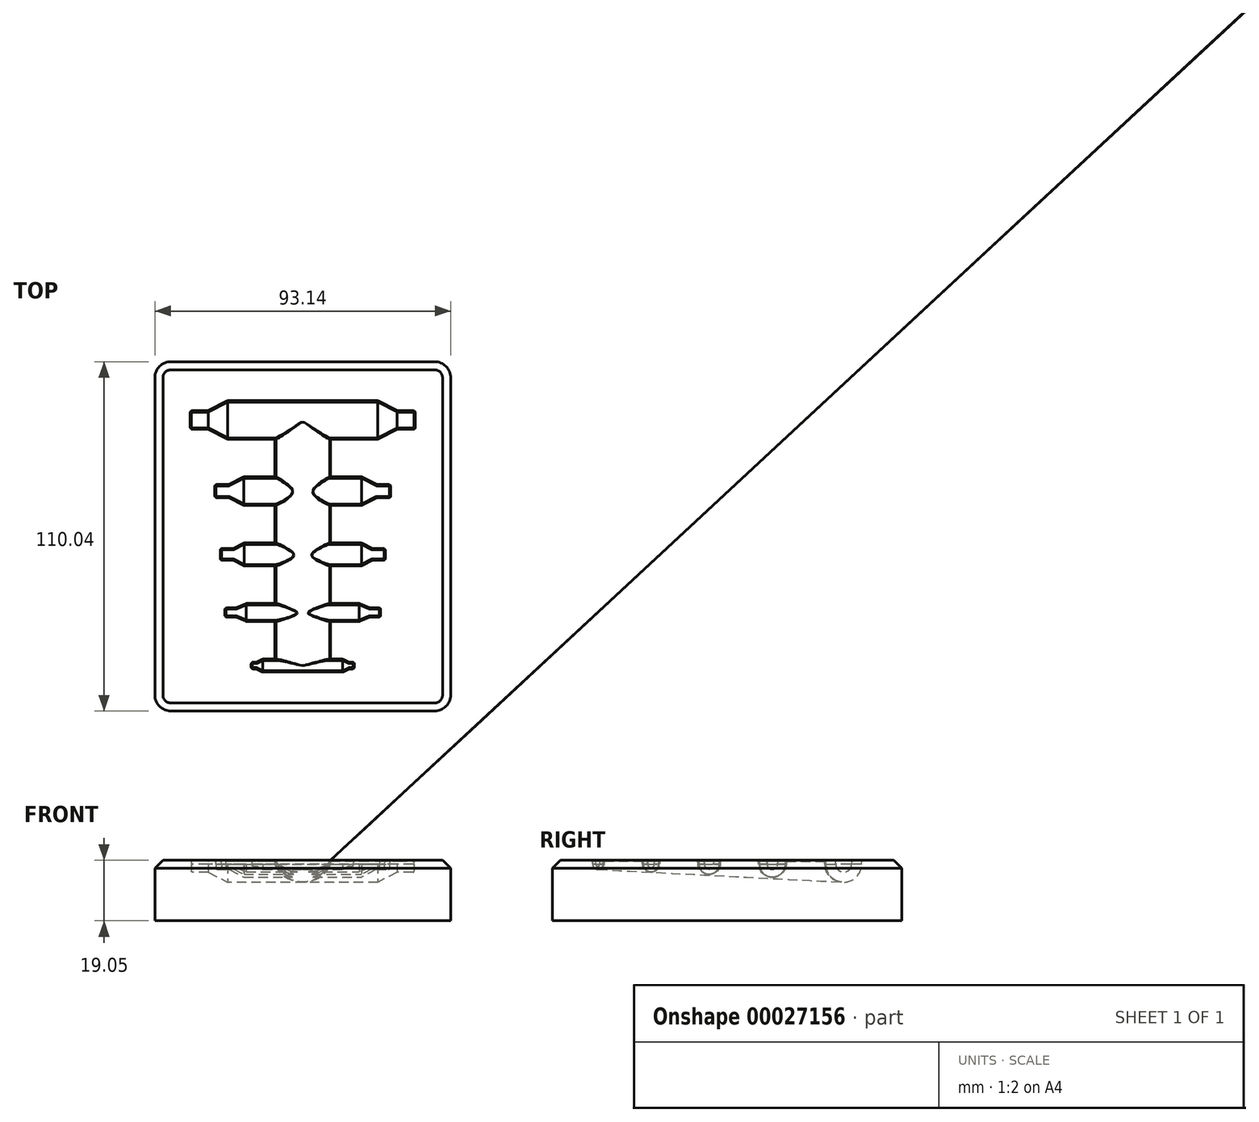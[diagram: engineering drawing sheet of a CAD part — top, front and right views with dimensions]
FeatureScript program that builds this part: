
annotation { "Feature Type Name" : "Feature", "Feature Type Description" : "" }
export const myFeature = defineFeature(function(context is Context, id is Id, definition is map)
    precondition{}
    {
        {
            var Q0;
            Q0=qCreatedBy(makeId("Top.planeOp"),FACE);
            var sketch = newSketch(context, id + "F0", { "sketchPlane" : qUnion([Q0])});
            skLineSegment(sketch, "E0.bottom", {"start": v(-46.57, 55.02) * mm, "end": v(46.57, 55.02) * mm});
            skLineSegment(sketch, "E0.top", {"start": v(-46.57, -55.02) * mm, "end": v(46.57, -55.02) * mm});
            skLineSegment(sketch, "E0.left", {"start": v(-46.57, 55.02) * mm, "end": v(-46.57, -55.02) * mm});
            skLineSegment(sketch, "E0.right", {"start": v(46.57, 55.02) * mm, "end": v(46.57, -55.02) * mm});
            skSolve(sketch);
        }
        {
            var Q0;
            Q0 = qSketchRegion(id + "F0", true);
            extrude(context, id + "F1", {"entities" : qUnion([Q0]), "depth" : 17.78 * mm});
        }
        {
            var Q0;
            Q0=makeQuery(id+"F1.opExtrude","CAP_FACE",FACE,{"disambiguationData":[OSD([sQuery(id+"F0.wireOp",EDGE,"E0.bottom"),sQuery(id+"F0.wireOp",EDGE,"E0.top"),sQuery(id+"F0.wireOp",EDGE,"E0.left"),sQuery(id+"F0.wireOp",EDGE,"E0.right")])],"isStart":false});
            var sketch = newSketch(context, id + "F2", { "sketchPlane" : qUnion([Q0])});
            skLineSegment(sketch, "E1", {"start": v(-15.88, -40.7) * mm, "end": v(-15.88, -41.34) * mm});
            skLineSegment(sketch, "E2", {"start": v(-15.87, -41.34) * mm, "end": v(-14.48, -41.34) * mm});
            skLineSegment(sketch, "E3", {"start": v(-14.48, -41.34) * mm, "end": v(-12.57, -42.32) * mm});
            skLineSegment(sketch, "E4", {"start": v(-12.57, -42.32) * mm, "end": v(0, -42.32) * mm});
            skLineSegment(sketch, "E5.MirrorCS", {"start": v(12.57, -42.32) * mm, "end": v(0, -42.32) * mm});
            skLineSegment(sketch, "E6.MirrorCS", {"start": v(14.48, -41.34) * mm, "end": v(12.57, -42.32) * mm});
            skLineSegment(sketch, "E7.MirrorCS", {"start": v(15.88, -40.7) * mm, "end": v(15.88, -41.34) * mm});
            skLineSegment(sketch, "E8.MirrorCS", {"start": v(15.87, -41.34) * mm, "end": v(14.48, -41.34) * mm});
            skLineSegment(sketch, "E9", {"start": v(-15.87, -40.7) * mm, "end": v(15.87, -40.7) * mm});
            skSolve(sketch);
        }
        {
            var Q0;
            Q0 = qSketchRegion(id + "F2", true);
            var Q1;
            Q1=sQuery(id+"F2.wireOp",EDGE,"E9");
            revolve(context, id + "F3", {"operationType" : NewBodyOperationType.REMOVE, "entities" : qUnion([Q0]), "axis" : qUnion([Q1]), "revolveType" : RevolveType.FULL, "oppositeDirection" : true});
        }
        {
            var Q0;
            Q0=makeQuery(id+"F1.opExtrude","CAP_FACE",FACE,{"disambiguationData":[OSD([sQuery(id+"F0.wireOp",EDGE,"E0.bottom"),sQuery(id+"F0.wireOp",EDGE,"E0.top"),sQuery(id+"F0.wireOp",EDGE,"E0.left"),sQuery(id+"F0.wireOp",EDGE,"E0.right")])],"isStart":false});
            var sketch = newSketch(context, id + "F4", { "sketchPlane" : qUnion([Q0])});
            skLineSegment(sketch, "E10", {"start": v(-24.13, -23.97) * mm, "end": v(-24.13, -25.01) * mm});
            skLineSegment(sketch, "E11", {"start": v(-24.13, -25.01) * mm, "end": v(-20.96, -25.01) * mm});
            skLineSegment(sketch, "E12", {"start": v(-20.96, -25.01) * mm, "end": v(-17.78, -26.38) * mm});
            skLineSegment(sketch, "E13", {"start": v(-17.78, -26.38) * mm, "end": v(0, -26.38) * mm});
            skLineSegment(sketch, "E14.MirrorCS", {"start": v(17.78, -26.38) * mm, "end": v(0, -26.38) * mm});
            skLineSegment(sketch, "E15.MirrorCS", {"start": v(20.96, -25.01) * mm, "end": v(17.78, -26.38) * mm});
            skLineSegment(sketch, "E16.MirrorCS", {"start": v(24.13, -23.97) * mm, "end": v(24.13, -25.01) * mm});
            skLineSegment(sketch, "E17.MirrorCS", {"start": v(24.13, -25.01) * mm, "end": v(20.96, -25.01) * mm});
            skLineSegment(sketch, "E18", {"start": v(-24.13, -23.97) * mm, "end": v(24.13, -23.97) * mm});
            skSolve(sketch);
        }
        {
            var Q0;
            Q0 = qSketchRegion(id + "F4", true);
            var Q1;
            Q1=sQuery(id+"F4.wireOp",EDGE,"E18");
            revolve(context, id + "F5", {"operationType" : NewBodyOperationType.REMOVE, "entities" : qUnion([Q0]), "axis" : qUnion([Q1]), "revolveType" : RevolveType.FULL, "oppositeDirection" : true});
        }
        {
            var Q0;
            Q0=makeQuery(id+"F1.opExtrude","CAP_FACE",FACE,{"disambiguationData":[OSD([sQuery(id+"F0.wireOp",EDGE,"E0.bottom"),sQuery(id+"F0.wireOp",EDGE,"E0.top"),sQuery(id+"F0.wireOp",EDGE,"E0.left"),sQuery(id+"F0.wireOp",EDGE,"E0.right")])],"isStart":false});
            var sketch = newSketch(context, id + "F6", { "sketchPlane" : qUnion([Q0])});
            skLineSegment(sketch, "E19", {"start": v(-25.6, -5.68) * mm, "end": v(-25.6, -7.14) * mm});
            skLineSegment(sketch, "E20", {"start": v(-25.6, -7.14) * mm, "end": v(-21.8, -7.14) * mm});
            skLineSegment(sketch, "E21", {"start": v(-21.8, -7.14) * mm, "end": v(-18.5, -8.86) * mm});
            skLineSegment(sketch, "E22", {"start": v(-18.5, -8.86) * mm, "end": v(0, -8.86) * mm});
            skLineSegment(sketch, "E23.MirrorCS", {"start": v(18.5, -8.86) * mm, "end": v(0, -8.86) * mm});
            skLineSegment(sketch, "E24.MirrorCS", {"start": v(21.8, -7.14) * mm, "end": v(18.5, -8.86) * mm});
            skLineSegment(sketch, "E25.MirrorCS", {"start": v(25.6, -5.68) * mm, "end": v(25.6, -7.14) * mm});
            skLineSegment(sketch, "E26.MirrorCS", {"start": v(25.6, -7.14) * mm, "end": v(21.8, -7.14) * mm});
            skLineSegment(sketch, "E27", {"start": v(-25.6, -5.68) * mm, "end": v(25.6, -5.68) * mm});
            skSolve(sketch);
        }
        {
            var Q0;
            Q0 = qSketchRegion(id + "F6", true);
            var Q1;
            Q1=sQuery(id+"F6.wireOp",EDGE,"E27");
            revolve(context, id + "F7", {"operationType" : NewBodyOperationType.REMOVE, "entities" : qUnion([Q0]), "axis" : qUnion([Q1]), "revolveType" : RevolveType.FULL, "oppositeDirection" : true});
        }
        {
            var Q0;
            Q0=makeQuery(id+"F1.opExtrude","CAP_FACE",FACE,{"disambiguationData":[OSD([sQuery(id+"F0.wireOp",EDGE,"E0.bottom"),sQuery(id+"F0.wireOp",EDGE,"E0.top"),sQuery(id+"F0.wireOp",EDGE,"E0.left"),sQuery(id+"F0.wireOp",EDGE,"E0.right")])],"isStart":false});
            var sketch = newSketch(context, id + "F8", { "sketchPlane" : qUnion([Q0])});
            skLineSegment(sketch, "E28", {"start": v(-27.3, 14.26) * mm, "end": v(-27.3, 12.6) * mm});
            skLineSegment(sketch, "E29", {"start": v(-27.3, 12.6) * mm, "end": v(-23.2, 12.6) * mm});
            skLineSegment(sketch, "E30", {"start": v(-23.2, 12.6) * mm, "end": v(-18.57, 10.2) * mm});
            skLineSegment(sketch, "E31", {"start": v(-18.57, 10.2) * mm, "end": v(0, 10.2) * mm});
            skLineSegment(sketch, "E32.MirrorCS", {"start": v(18.57, 10.2) * mm, "end": v(0, 10.2) * mm});
            skLineSegment(sketch, "E33.MirrorCS", {"start": v(23.2, 12.6) * mm, "end": v(18.57, 10.2) * mm});
            skLineSegment(sketch, "E34.MirrorCS", {"start": v(27.3, 14.26) * mm, "end": v(27.3, 12.6) * mm});
            skLineSegment(sketch, "E35.MirrorCS", {"start": v(27.3, 12.6) * mm, "end": v(23.2, 12.6) * mm});
            skLineSegment(sketch, "E36", {"start": v(-27.3, 14.26) * mm, "end": v(27.3, 14.26) * mm});
            skSolve(sketch);
        }
        {
            var Q0;
            Q0 = qSketchRegion(id + "F8", true);
            var Q1;
            Q1=sQuery(id+"F8.wireOp",EDGE,"E36");
            revolve(context, id + "F9", {"operationType" : NewBodyOperationType.REMOVE, "entities" : qUnion([Q0]), "axis" : qUnion([Q1]), "revolveType" : RevolveType.FULL, "oppositeDirection" : true});
        }
        {
            var Q0;
            Q0=makeQuery(id+"F1.opExtrude","CAP_FACE",FACE,{"disambiguationData":[OSD([sQuery(id+"F0.wireOp",EDGE,"E0.bottom"),sQuery(id+"F0.wireOp",EDGE,"E0.top"),sQuery(id+"F0.wireOp",EDGE,"E0.left"),sQuery(id+"F0.wireOp",EDGE,"E0.right")])],"isStart":false});
            var sketch = newSketch(context, id + "F10", { "sketchPlane" : qUnion([Q0])});
            skLineSegment(sketch, "E37", {"start": v(-35.05, 36.67) * mm, "end": v(-35.05, 34.2) * mm});
            skLineSegment(sketch, "E38", {"start": v(-35.05, 34.2) * mm, "end": v(-29.72, 34.2) * mm});
            skLineSegment(sketch, "E39", {"start": v(-29.72, 34.2) * mm, "end": v(-23.62, 31.02) * mm});
            skLineSegment(sketch, "E40", {"start": v(-23.62, 31.02) * mm, "end": v(0, 31.02) * mm});
            skLineSegment(sketch, "E41.MirrorCS", {"start": v(23.62, 31.02) * mm, "end": v(0, 31.02) * mm});
            skLineSegment(sketch, "E42.MirrorCS", {"start": v(29.72, 34.2) * mm, "end": v(23.62, 31.02) * mm});
            skLineSegment(sketch, "E43.MirrorCS", {"start": v(35.05, 36.67) * mm, "end": v(35.05, 34.2) * mm});
            skLineSegment(sketch, "E44.MirrorCS", {"start": v(35.05, 34.2) * mm, "end": v(29.72, 34.2) * mm});
            skLineSegment(sketch, "E45", {"start": v(-35.05, 36.67) * mm, "end": v(35.05, 36.67) * mm});
            skSolve(sketch);
        }
        {
            var Q0;
            Q0 = qSketchRegion(id + "F10", true);
            var Q1;
            Q1=sQuery(id+"F10.wireOp",EDGE,"E45");
            revolve(context, id + "F11", {"operationType" : NewBodyOperationType.REMOVE, "entities" : qUnion([Q0]), "axis" : qUnion([Q1]), "revolveType" : RevolveType.FULL});
        }
        {
            var Q0;
            Q0=sQuery(id+"F2.wireOp",EDGE,"E9");
            cPlane(context, id + "F12", {"entities" : qUnion([Q0]), "cplaneType" : CPlaneType.LINE_ANGLE, "offset" : 152.4 * mm, "angle" : 0 * degree, "width" : 152.4 * mm, "height" : 152.4 * mm});
        }
        {
            var Q0;
            Q0=sQuery(id+"F10.wireOp",EDGE,"E45");
            cPlane(context, id + "F13", {"entities" : qUnion([Q0]), "cplaneType" : CPlaneType.LINE_ANGLE, "offset" : 152.4 * mm, "angle" : 0 * degree, "width" : 152.4 * mm, "height" : 152.4 * mm});
        }
        {
            var Q0;
            Q0=makeQuery(id+"F1.opExtrude","CAP_FACE",FACE,{"disambiguationData":[OSD([sQuery(id+"F0.wireOp",EDGE,"E0.bottom"),sQuery(id+"F0.wireOp",EDGE,"E0.top"),sQuery(id+"F0.wireOp",EDGE,"E0.left"),sQuery(id+"F0.wireOp",EDGE,"E0.right")])],"isStart":false});
            extrude(context, id + "F14", {"entities" : qUnion([Q0]), "operationType" : NewBodyOperationType.ADD, "depth" : 1.27 * mm, "hasDraft" : true, "draftAngle" : 5 * degree, "draftPullDirection" : true});
        }
        {
            var Q0;
            Q0=qCreatedBy(id+"F12.planeOp",FACE);
            var sketch = newSketch(context, id + "F15", { "sketchPlane" : qUnion([Q0])});
            skEllipse(sketch, "E46", {"center": v(0, 19.05) * mm, "majorRadius": 8.47 * mm, "minorRadius": 2.89 * mm, "majorAxis": v(-1, 0)});
            skSolve(sketch);
        }
        {
            var Q0;
            Q0=qCreatedBy(id+"F13.planeOp",FACE);
            var sketch = newSketch(context, id + "F16", { "sketchPlane" : qUnion([Q0])});
            skEllipse(sketch, "E47", {"center": v(0, 19.05) * mm, "majorRadius": 8.47 * mm, "minorRadius": 6.92 * mm, "majorAxis": v(-1, 0)});
            skSolve(sketch);
        }
        {
            var Q1;
            Q1 = qSketchRegion(id + "F15", true);
            var Q2;
            Q2 = qSketchRegion(id + "F16", true);
            loft(context, id + "F17", {"operationType" : NewBodyOperationType.REMOVE, "sheetProfilesArray" : [{ "sheetProfileEntities" : qUnion([Q1]) }, { "sheetProfileEntities" : qUnion([Q2]) }]});
        }
        {
            var Q0;
            Q0=makeQuery(id+"F1.opExtrude","SWEPT_EDGE",EDGE,{"disambiguationData":[OSD([sQuery(id+"F0.wireOp",EDGE,"E0.top"),sQuery(id+"F0.wireOp",EDGE,"E0.left")])]});
            var Q1;
            Q1=makeQuery(id+"F1.opExtrude","SWEPT_EDGE",EDGE,{"disambiguationData":[OSD([sQuery(id+"F0.wireOp",EDGE,"E0.top"),sQuery(id+"F0.wireOp",EDGE,"E0.right")])]});
            var Q2;
            Q2=makeQuery(id+"F1.opExtrude","SWEPT_EDGE",EDGE,{"disambiguationData":[OSD([sQuery(id+"F0.wireOp",EDGE,"E0.bottom"),sQuery(id+"F0.wireOp",EDGE,"E0.right")])]});
            var Q3;
            Q3=makeQuery(id+"F1.opExtrude","SWEPT_EDGE",EDGE,{"disambiguationData":[OSD([sQuery(id+"F0.wireOp",EDGE,"E0.bottom"),sQuery(id+"F0.wireOp",EDGE,"E0.left")])]});
            var Q4;
            Q4=makeQuery(id+"F14.opExtrude","SWEPT_EDGE",EDGE,{"disambiguationData":[OSD([sQuery(id+"F0.wireOp",EDGE,"E0.top"),sQuery(id+"F0.wireOp",EDGE,"E0.right")])]});
            var Q5;
            Q5=makeQuery(id+"F14.opExtrude","SWEPT_EDGE",EDGE,{"disambiguationData":[OSD([sQuery(id+"F0.wireOp",EDGE,"E0.bottom"),sQuery(id+"F0.wireOp",EDGE,"E0.right")])]});
            var Q6;
            Q6=makeQuery(id+"F14.opExtrude","SWEPT_EDGE",EDGE,{"disambiguationData":[OSD([sQuery(id+"F0.wireOp",EDGE,"E0.bottom"),sQuery(id+"F0.wireOp",EDGE,"E0.left")])]});
            var Q7;
            Q7=makeQuery(id+"F14.opExtrude","SWEPT_EDGE",EDGE,{"disambiguationData":[OSD([sQuery(id+"F0.wireOp",EDGE,"E0.top"),sQuery(id+"F0.wireOp",EDGE,"E0.left")])]});
            fillet(context, id + "F18", {"entities" : qUnion([Q0, Q1, Q2, Q3, Q4, Q5, Q6, Q7]), "radius" : 5.08 * mm, "tangentPropagation" : true, "allowEdgeOverflow" : false});
        }
        {
            var Q0;
            Q0=makeQuery(id+"F14.opExtrude","CAP_EDGE",EDGE,{"disambiguationData":[OSD([sQuery(id+"F0.wireOp",EDGE,"E0.left")])],"isStart":false});
            chamfer(context, id + "F19", {"entities" : qUnion([Q0]), "width" : 2.54 * mm, "tangentPropagation" : true});
        }
        {
            var Q0;
            Q0=makeQuery(id+"F17.boolean.opBoolean","INTERSECT",EDGE,{"disambiguationData":[OD(0.0)],"derivedFrom":[makeQuery(id+"F5.boolean.opBoolean","COPY",FACE,{"derivedFrom":makeQuery(id+"F5.opRevolve","SWEPT_FACE",FACE,{"disambiguationData":[OSD([sQuery(id+"F4.wireOp",EDGE,"E13"),sQuery(id+"F4.wireOp",EDGE,"E14.MirrorCS")])]})}),makeQuery(id+"F17.opLoft","SWEPT_FACE",FACE,{"disambiguationData":[OSD([sQuery(id+"F15.wireOp",EDGE,"E46"),sQuery(id+"F16.wireOp",EDGE,"E47")])]})]});
            var Q1;
            {var subQ0=sQuery(id+"F0.wireOp",EDGE,"E0.bottom");var subQ1=sQuery(id+"F0.wireOp",EDGE,"E0.top");var subQ2=sQuery(id+"F0.wireOp",EDGE,"E0.left");var subQ3=sQuery(id+"F0.wireOp",EDGE,"E0.right");var subQ4=sQuery(id+"F4.wireOp",EDGE,"E13");var subQ5=sQuery(id+"F4.wireOp",EDGE,"E14.MirrorCS");Q1=makeQuery(id+"F17.boolean.opBoolean","INTERSECT",EDGE,{"disambiguationData":[OD(0.0)],"derivedFrom":[makeQuery(id+"F14.opExtrude","SWEPT_FACE",FACE,{"disambiguationData":[OSD([subQ0,subQ1,subQ2,subQ3,subQ4,subQ5]),TDD([makeQuery(id+"F5.boolean.opBoolean","INTERSECT",EDGE,{"disambiguationData":[OD(1.0)],"derivedFrom":[makeQuery(id+"F1.opExtrude","CAP_FACE",FACE,{"disambiguationData":[OSD([subQ0,subQ1,subQ2,subQ3])],"isStart":false}),makeQuery(id+"F5.opRevolve","SWEPT_FACE",FACE,{"disambiguationData":[OSD([subQ4,subQ5])]})]})])]}),makeQuery(id+"F17.opLoft","SWEPT_FACE",FACE,{"disambiguationData":[OSD([sQuery(id+"F15.wireOp",EDGE,"E46"),sQuery(id+"F16.wireOp",EDGE,"E47")])]})]});}
            var Q2;
            {var subQ0=sQuery(id+"F0.wireOp",EDGE,"E0.bottom");var subQ1=sQuery(id+"F0.wireOp",EDGE,"E0.top");var subQ2=sQuery(id+"F0.wireOp",EDGE,"E0.left");var subQ3=sQuery(id+"F0.wireOp",EDGE,"E0.right");var subQ4=sQuery(id+"F4.wireOp",EDGE,"E13");var subQ5=sQuery(id+"F4.wireOp",EDGE,"E14.MirrorCS");Q2=makeQuery(id+"F17.boolean.opBoolean","INTERSECT",EDGE,{"disambiguationData":[OD(0.0)],"derivedFrom":[makeQuery(id+"F14.opExtrude","SWEPT_FACE",FACE,{"disambiguationData":[OSD([subQ0,subQ1,subQ2,subQ3,subQ4,subQ5]),TDD([makeQuery(id+"F5.boolean.opBoolean","INTERSECT",EDGE,{"disambiguationData":[OD(0.0)],"derivedFrom":[makeQuery(id+"F1.opExtrude","CAP_FACE",FACE,{"disambiguationData":[OSD([subQ0,subQ1,subQ2,subQ3])],"isStart":false}),makeQuery(id+"F5.opRevolve","SWEPT_FACE",FACE,{"disambiguationData":[OSD([subQ4,subQ5])]})]})])]}),makeQuery(id+"F17.opLoft","SWEPT_FACE",FACE,{"disambiguationData":[OSD([sQuery(id+"F15.wireOp",EDGE,"E46"),sQuery(id+"F16.wireOp",EDGE,"E47")])]})]});}
            var Q3;
            Q3=makeQuery(id+"F17.boolean.opBoolean","INTERSECT",EDGE,{"derivedFrom":[makeQuery(id+"F3.boolean.opBoolean","COPY",FACE,{"derivedFrom":makeQuery(id+"F3.opRevolve","SWEPT_FACE",FACE,{"disambiguationData":[OSD([sQuery(id+"F2.wireOp",EDGE,"E4"),sQuery(id+"F2.wireOp",EDGE,"E5.MirrorCS")])]})}),makeQuery(id+"F17.opLoft","SWEPT_FACE",FACE,{"disambiguationData":[OSD([sQuery(id+"F15.wireOp",EDGE,"E46"),sQuery(id+"F16.wireOp",EDGE,"E47")])]})]});
            var Q4;
            {var subQ0=sQuery(id+"F0.wireOp",EDGE,"E0.bottom");var subQ1=sQuery(id+"F0.wireOp",EDGE,"E0.top");var subQ2=sQuery(id+"F0.wireOp",EDGE,"E0.left");var subQ3=sQuery(id+"F0.wireOp",EDGE,"E0.right");var subQ4=sQuery(id+"F2.wireOp",EDGE,"E4");var subQ5=sQuery(id+"F2.wireOp",EDGE,"E5.MirrorCS");Q4=makeQuery(id+"F17.boolean.opBoolean","INTERSECT",EDGE,{"disambiguationData":[OD(0.0)],"derivedFrom":[makeQuery(id+"F14.opExtrude","SWEPT_FACE",FACE,{"disambiguationData":[OSD([subQ0,subQ1,subQ2,subQ3,subQ4,subQ5]),TDD([makeQuery(id+"F3.boolean.opBoolean","INTERSECT",EDGE,{"disambiguationData":[OD(1.0)],"derivedFrom":[makeQuery(id+"F1.opExtrude","CAP_FACE",FACE,{"disambiguationData":[OSD([subQ0,subQ1,subQ2,subQ3])],"isStart":false}),makeQuery(id+"F3.opRevolve","SWEPT_FACE",FACE,{"disambiguationData":[OSD([subQ4,subQ5])]})]})])]}),makeQuery(id+"F17.opLoft","SWEPT_FACE",FACE,{"disambiguationData":[OSD([sQuery(id+"F15.wireOp",EDGE,"E46"),sQuery(id+"F16.wireOp",EDGE,"E47")])]})]});}
            var Q5;
            {var subQ0=sQuery(id+"F0.wireOp",EDGE,"E0.bottom");var subQ1=sQuery(id+"F0.wireOp",EDGE,"E0.top");var subQ2=sQuery(id+"F0.wireOp",EDGE,"E0.left");var subQ3=sQuery(id+"F0.wireOp",EDGE,"E0.right");var subQ4=sQuery(id+"F2.wireOp",EDGE,"E4");var subQ5=sQuery(id+"F2.wireOp",EDGE,"E5.MirrorCS");Q5=makeQuery(id+"F17.boolean.opBoolean","INTERSECT",EDGE,{"disambiguationData":[OD(1.0)],"derivedFrom":[makeQuery(id+"F14.opExtrude","SWEPT_FACE",FACE,{"disambiguationData":[OSD([subQ0,subQ1,subQ2,subQ3,subQ4,subQ5]),TDD([makeQuery(id+"F3.boolean.opBoolean","INTERSECT",EDGE,{"disambiguationData":[OD(1.0)],"derivedFrom":[makeQuery(id+"F1.opExtrude","CAP_FACE",FACE,{"disambiguationData":[OSD([subQ0,subQ1,subQ2,subQ3])],"isStart":false}),makeQuery(id+"F3.opRevolve","SWEPT_FACE",FACE,{"disambiguationData":[OSD([subQ4,subQ5])]})]})])]}),makeQuery(id+"F17.opLoft","SWEPT_FACE",FACE,{"disambiguationData":[OSD([sQuery(id+"F15.wireOp",EDGE,"E46"),sQuery(id+"F16.wireOp",EDGE,"E47")])]})]});}
            var Q6;
            Q6=makeQuery(id+"F17.boolean.opBoolean","INTERSECT",EDGE,{"disambiguationData":[OD(1.0)],"derivedFrom":[makeQuery(id+"F5.boolean.opBoolean","COPY",FACE,{"derivedFrom":makeQuery(id+"F5.opRevolve","SWEPT_FACE",FACE,{"disambiguationData":[OSD([sQuery(id+"F4.wireOp",EDGE,"E13"),sQuery(id+"F4.wireOp",EDGE,"E14.MirrorCS")])]})}),makeQuery(id+"F17.opLoft","SWEPT_FACE",FACE,{"disambiguationData":[OSD([sQuery(id+"F15.wireOp",EDGE,"E46"),sQuery(id+"F16.wireOp",EDGE,"E47")])]})]});
            var Q7;
            {var subQ0=sQuery(id+"F0.wireOp",EDGE,"E0.bottom");var subQ1=sQuery(id+"F0.wireOp",EDGE,"E0.top");var subQ2=sQuery(id+"F0.wireOp",EDGE,"E0.left");var subQ3=sQuery(id+"F0.wireOp",EDGE,"E0.right");var subQ4=sQuery(id+"F4.wireOp",EDGE,"E13");var subQ5=sQuery(id+"F4.wireOp",EDGE,"E14.MirrorCS");Q7=makeQuery(id+"F17.boolean.opBoolean","INTERSECT",EDGE,{"disambiguationData":[OD(1.0)],"derivedFrom":[makeQuery(id+"F14.opExtrude","SWEPT_FACE",FACE,{"disambiguationData":[OSD([subQ0,subQ1,subQ2,subQ3,subQ4,subQ5]),TDD([makeQuery(id+"F5.boolean.opBoolean","INTERSECT",EDGE,{"disambiguationData":[OD(1.0)],"derivedFrom":[makeQuery(id+"F1.opExtrude","CAP_FACE",FACE,{"disambiguationData":[OSD([subQ0,subQ1,subQ2,subQ3])],"isStart":false}),makeQuery(id+"F5.opRevolve","SWEPT_FACE",FACE,{"disambiguationData":[OSD([subQ4,subQ5])]})]})])]}),makeQuery(id+"F17.opLoft","SWEPT_FACE",FACE,{"disambiguationData":[OSD([sQuery(id+"F15.wireOp",EDGE,"E46"),sQuery(id+"F16.wireOp",EDGE,"E47")])]})]});}
            var Q8;
            {var subQ0=sQuery(id+"F0.wireOp",EDGE,"E0.bottom");var subQ1=sQuery(id+"F0.wireOp",EDGE,"E0.top");var subQ2=sQuery(id+"F0.wireOp",EDGE,"E0.left");var subQ3=sQuery(id+"F0.wireOp",EDGE,"E0.right");var subQ4=sQuery(id+"F4.wireOp",EDGE,"E13");var subQ5=sQuery(id+"F4.wireOp",EDGE,"E14.MirrorCS");Q8=makeQuery(id+"F17.boolean.opBoolean","INTERSECT",EDGE,{"disambiguationData":[OD(1.0)],"derivedFrom":[makeQuery(id+"F14.opExtrude","SWEPT_FACE",FACE,{"disambiguationData":[OSD([subQ0,subQ1,subQ2,subQ3,subQ4,subQ5]),TDD([makeQuery(id+"F5.boolean.opBoolean","INTERSECT",EDGE,{"disambiguationData":[OD(0.0)],"derivedFrom":[makeQuery(id+"F1.opExtrude","CAP_FACE",FACE,{"disambiguationData":[OSD([subQ0,subQ1,subQ2,subQ3])],"isStart":false}),makeQuery(id+"F5.opRevolve","SWEPT_FACE",FACE,{"disambiguationData":[OSD([subQ4,subQ5])]})]})])]}),makeQuery(id+"F17.opLoft","SWEPT_FACE",FACE,{"disambiguationData":[OSD([sQuery(id+"F15.wireOp",EDGE,"E46"),sQuery(id+"F16.wireOp",EDGE,"E47")])]})]});}
            var Q9;
            {var subQ0=sQuery(id+"F0.wireOp",EDGE,"E0.bottom");var subQ1=sQuery(id+"F0.wireOp",EDGE,"E0.top");var subQ2=sQuery(id+"F0.wireOp",EDGE,"E0.left");var subQ3=sQuery(id+"F0.wireOp",EDGE,"E0.right");var subQ4=sQuery(id+"F6.wireOp",EDGE,"E22");var subQ5=sQuery(id+"F6.wireOp",EDGE,"E23.MirrorCS");Q9=makeQuery(id+"F17.boolean.opBoolean","INTERSECT",EDGE,{"disambiguationData":[OD(1.0)],"derivedFrom":[makeQuery(id+"F14.opExtrude","SWEPT_FACE",FACE,{"disambiguationData":[OSD([subQ0,subQ1,subQ2,subQ3,subQ4,subQ5]),TDD([makeQuery(id+"F7.boolean.opBoolean","INTERSECT",EDGE,{"disambiguationData":[OD(1.0)],"derivedFrom":[makeQuery(id+"F1.opExtrude","CAP_FACE",FACE,{"disambiguationData":[OSD([subQ0,subQ1,subQ2,subQ3])],"isStart":false}),makeQuery(id+"F7.opRevolve","SWEPT_FACE",FACE,{"disambiguationData":[OSD([subQ4,subQ5])]})]})])]}),makeQuery(id+"F17.opLoft","SWEPT_FACE",FACE,{"disambiguationData":[OSD([sQuery(id+"F15.wireOp",EDGE,"E46"),sQuery(id+"F16.wireOp",EDGE,"E47")])]})]});}
            var Q10;
            Q10=makeQuery(id+"F17.boolean.opBoolean","INTERSECT",EDGE,{"disambiguationData":[OD(1.0)],"derivedFrom":[makeQuery(id+"F7.boolean.opBoolean","COPY",FACE,{"derivedFrom":makeQuery(id+"F7.opRevolve","SWEPT_FACE",FACE,{"disambiguationData":[OSD([sQuery(id+"F6.wireOp",EDGE,"E22"),sQuery(id+"F6.wireOp",EDGE,"E23.MirrorCS")])]})}),makeQuery(id+"F17.opLoft","SWEPT_FACE",FACE,{"disambiguationData":[OSD([sQuery(id+"F15.wireOp",EDGE,"E46"),sQuery(id+"F16.wireOp",EDGE,"E47")])]})]});
            var Q11;
            {var subQ0=sQuery(id+"F0.wireOp",EDGE,"E0.bottom");var subQ1=sQuery(id+"F0.wireOp",EDGE,"E0.top");var subQ2=sQuery(id+"F0.wireOp",EDGE,"E0.left");var subQ3=sQuery(id+"F0.wireOp",EDGE,"E0.right");var subQ4=sQuery(id+"F6.wireOp",EDGE,"E22");var subQ5=sQuery(id+"F6.wireOp",EDGE,"E23.MirrorCS");Q11=makeQuery(id+"F17.boolean.opBoolean","INTERSECT",EDGE,{"disambiguationData":[OD(1.0)],"derivedFrom":[makeQuery(id+"F14.opExtrude","SWEPT_FACE",FACE,{"disambiguationData":[OSD([subQ0,subQ1,subQ2,subQ3,subQ4,subQ5]),TDD([makeQuery(id+"F7.boolean.opBoolean","INTERSECT",EDGE,{"disambiguationData":[OD(0.0)],"derivedFrom":[makeQuery(id+"F1.opExtrude","CAP_FACE",FACE,{"disambiguationData":[OSD([subQ0,subQ1,subQ2,subQ3])],"isStart":false}),makeQuery(id+"F7.opRevolve","SWEPT_FACE",FACE,{"disambiguationData":[OSD([subQ4,subQ5])]})]})])]}),makeQuery(id+"F17.opLoft","SWEPT_FACE",FACE,{"disambiguationData":[OSD([sQuery(id+"F15.wireOp",EDGE,"E46"),sQuery(id+"F16.wireOp",EDGE,"E47")])]})]});}
            var Q12;
            Q12=makeQuery(id+"F17.boolean.opBoolean","INTERSECT",EDGE,{"disambiguationData":[OD(1.0)],"derivedFrom":[makeQuery(id+"F9.boolean.opBoolean","COPY",FACE,{"derivedFrom":makeQuery(id+"F9.opRevolve","SWEPT_FACE",FACE,{"disambiguationData":[OSD([sQuery(id+"F8.wireOp",EDGE,"E31"),sQuery(id+"F8.wireOp",EDGE,"E32.MirrorCS")])]})}),makeQuery(id+"F17.opLoft","SWEPT_FACE",FACE,{"disambiguationData":[OSD([sQuery(id+"F15.wireOp",EDGE,"E46"),sQuery(id+"F16.wireOp",EDGE,"E47")])]})]});
            var Q13;
            {var subQ0=sQuery(id+"F0.wireOp",EDGE,"E0.bottom");var subQ1=sQuery(id+"F0.wireOp",EDGE,"E0.top");var subQ2=sQuery(id+"F0.wireOp",EDGE,"E0.left");var subQ3=sQuery(id+"F0.wireOp",EDGE,"E0.right");var subQ4=sQuery(id+"F8.wireOp",EDGE,"E31");var subQ5=sQuery(id+"F8.wireOp",EDGE,"E32.MirrorCS");Q13=makeQuery(id+"F17.boolean.opBoolean","INTERSECT",EDGE,{"disambiguationData":[OD(1.0)],"derivedFrom":[makeQuery(id+"F14.opExtrude","SWEPT_FACE",FACE,{"disambiguationData":[OSD([subQ0,subQ1,subQ2,subQ3,subQ4,subQ5]),TDD([makeQuery(id+"F9.boolean.opBoolean","INTERSECT",EDGE,{"disambiguationData":[OD(0.0)],"derivedFrom":[makeQuery(id+"F1.opExtrude","CAP_FACE",FACE,{"disambiguationData":[OSD([subQ0,subQ1,subQ2,subQ3])],"isStart":false}),makeQuery(id+"F9.opRevolve","SWEPT_FACE",FACE,{"disambiguationData":[OSD([subQ4,subQ5])]})]})])]}),makeQuery(id+"F17.opLoft","SWEPT_FACE",FACE,{"disambiguationData":[OSD([sQuery(id+"F15.wireOp",EDGE,"E46"),sQuery(id+"F16.wireOp",EDGE,"E47")])]})]});}
            var Q14;
            {var subQ0=sQuery(id+"F0.wireOp",EDGE,"E0.bottom");var subQ1=sQuery(id+"F0.wireOp",EDGE,"E0.top");var subQ2=sQuery(id+"F0.wireOp",EDGE,"E0.left");var subQ3=sQuery(id+"F0.wireOp",EDGE,"E0.right");var subQ4=sQuery(id+"F8.wireOp",EDGE,"E31");var subQ5=sQuery(id+"F8.wireOp",EDGE,"E32.MirrorCS");Q14=makeQuery(id+"F17.boolean.opBoolean","INTERSECT",EDGE,{"disambiguationData":[OD(1.0)],"derivedFrom":[makeQuery(id+"F14.opExtrude","SWEPT_FACE",FACE,{"disambiguationData":[OSD([subQ0,subQ1,subQ2,subQ3,subQ4,subQ5]),TDD([makeQuery(id+"F9.boolean.opBoolean","INTERSECT",EDGE,{"disambiguationData":[OD(1.0)],"derivedFrom":[makeQuery(id+"F1.opExtrude","CAP_FACE",FACE,{"disambiguationData":[OSD([subQ0,subQ1,subQ2,subQ3])],"isStart":false}),makeQuery(id+"F9.opRevolve","SWEPT_FACE",FACE,{"disambiguationData":[OSD([subQ4,subQ5])]})]})])]}),makeQuery(id+"F17.opLoft","SWEPT_FACE",FACE,{"disambiguationData":[OSD([sQuery(id+"F15.wireOp",EDGE,"E46"),sQuery(id+"F16.wireOp",EDGE,"E47")])]})]});}
            var Q15;
            Q15=makeQuery(id+"F17.boolean.opBoolean","INTERSECT",EDGE,{"disambiguationData":[OD(0.0)],"derivedFrom":[makeQuery(id+"F9.boolean.opBoolean","COPY",FACE,{"derivedFrom":makeQuery(id+"F9.opRevolve","SWEPT_FACE",FACE,{"disambiguationData":[OSD([sQuery(id+"F8.wireOp",EDGE,"E31"),sQuery(id+"F8.wireOp",EDGE,"E32.MirrorCS")])]})}),makeQuery(id+"F17.opLoft","SWEPT_FACE",FACE,{"disambiguationData":[OSD([sQuery(id+"F15.wireOp",EDGE,"E46"),sQuery(id+"F16.wireOp",EDGE,"E47")])]})]});
            var Q16;
            {var subQ0=sQuery(id+"F0.wireOp",EDGE,"E0.bottom");var subQ1=sQuery(id+"F0.wireOp",EDGE,"E0.top");var subQ2=sQuery(id+"F0.wireOp",EDGE,"E0.left");var subQ3=sQuery(id+"F0.wireOp",EDGE,"E0.right");var subQ4=sQuery(id+"F8.wireOp",EDGE,"E31");var subQ5=sQuery(id+"F8.wireOp",EDGE,"E32.MirrorCS");Q16=makeQuery(id+"F17.boolean.opBoolean","INTERSECT",EDGE,{"disambiguationData":[OD(0.0)],"derivedFrom":[makeQuery(id+"F14.opExtrude","SWEPT_FACE",FACE,{"disambiguationData":[OSD([subQ0,subQ1,subQ2,subQ3,subQ4,subQ5]),TDD([makeQuery(id+"F9.boolean.opBoolean","INTERSECT",EDGE,{"disambiguationData":[OD(1.0)],"derivedFrom":[makeQuery(id+"F1.opExtrude","CAP_FACE",FACE,{"disambiguationData":[OSD([subQ0,subQ1,subQ2,subQ3])],"isStart":false}),makeQuery(id+"F9.opRevolve","SWEPT_FACE",FACE,{"disambiguationData":[OSD([subQ4,subQ5])]})]})])]}),makeQuery(id+"F17.opLoft","SWEPT_FACE",FACE,{"disambiguationData":[OSD([sQuery(id+"F15.wireOp",EDGE,"E46"),sQuery(id+"F16.wireOp",EDGE,"E47")])]})]});}
            var Q17;
            {var subQ0=sQuery(id+"F0.wireOp",EDGE,"E0.bottom");var subQ1=sQuery(id+"F0.wireOp",EDGE,"E0.top");var subQ2=sQuery(id+"F0.wireOp",EDGE,"E0.left");var subQ3=sQuery(id+"F0.wireOp",EDGE,"E0.right");var subQ4=sQuery(id+"F8.wireOp",EDGE,"E31");var subQ5=sQuery(id+"F8.wireOp",EDGE,"E32.MirrorCS");Q17=makeQuery(id+"F17.boolean.opBoolean","INTERSECT",EDGE,{"disambiguationData":[OD(0.0)],"derivedFrom":[makeQuery(id+"F14.opExtrude","SWEPT_FACE",FACE,{"disambiguationData":[OSD([subQ0,subQ1,subQ2,subQ3,subQ4,subQ5]),TDD([makeQuery(id+"F9.boolean.opBoolean","INTERSECT",EDGE,{"disambiguationData":[OD(0.0)],"derivedFrom":[makeQuery(id+"F1.opExtrude","CAP_FACE",FACE,{"disambiguationData":[OSD([subQ0,subQ1,subQ2,subQ3])],"isStart":false}),makeQuery(id+"F9.opRevolve","SWEPT_FACE",FACE,{"disambiguationData":[OSD([subQ4,subQ5])]})]})])]}),makeQuery(id+"F17.opLoft","SWEPT_FACE",FACE,{"disambiguationData":[OSD([sQuery(id+"F15.wireOp",EDGE,"E46"),sQuery(id+"F16.wireOp",EDGE,"E47")])]})]});}
            var Q18;
            {var subQ0=sQuery(id+"F0.wireOp",EDGE,"E0.bottom");var subQ1=sQuery(id+"F0.wireOp",EDGE,"E0.top");var subQ2=sQuery(id+"F0.wireOp",EDGE,"E0.left");var subQ3=sQuery(id+"F0.wireOp",EDGE,"E0.right");var subQ4=sQuery(id+"F6.wireOp",EDGE,"E22");var subQ5=sQuery(id+"F6.wireOp",EDGE,"E23.MirrorCS");Q18=makeQuery(id+"F17.boolean.opBoolean","INTERSECT",EDGE,{"disambiguationData":[OD(0.0)],"derivedFrom":[makeQuery(id+"F14.opExtrude","SWEPT_FACE",FACE,{"disambiguationData":[OSD([subQ0,subQ1,subQ2,subQ3,subQ4,subQ5]),TDD([makeQuery(id+"F7.boolean.opBoolean","INTERSECT",EDGE,{"disambiguationData":[OD(1.0)],"derivedFrom":[makeQuery(id+"F1.opExtrude","CAP_FACE",FACE,{"disambiguationData":[OSD([subQ0,subQ1,subQ2,subQ3])],"isStart":false}),makeQuery(id+"F7.opRevolve","SWEPT_FACE",FACE,{"disambiguationData":[OSD([subQ4,subQ5])]})]})])]}),makeQuery(id+"F17.opLoft","SWEPT_FACE",FACE,{"disambiguationData":[OSD([sQuery(id+"F15.wireOp",EDGE,"E46"),sQuery(id+"F16.wireOp",EDGE,"E47")])]})]});}
            var Q19;
            Q19=makeQuery(id+"F17.boolean.opBoolean","INTERSECT",EDGE,{"disambiguationData":[OD(0.0)],"derivedFrom":[makeQuery(id+"F7.boolean.opBoolean","COPY",FACE,{"derivedFrom":makeQuery(id+"F7.opRevolve","SWEPT_FACE",FACE,{"disambiguationData":[OSD([sQuery(id+"F6.wireOp",EDGE,"E22"),sQuery(id+"F6.wireOp",EDGE,"E23.MirrorCS")])]})}),makeQuery(id+"F17.opLoft","SWEPT_FACE",FACE,{"disambiguationData":[OSD([sQuery(id+"F15.wireOp",EDGE,"E46"),sQuery(id+"F16.wireOp",EDGE,"E47")])]})]});
            var Q20;
            {var subQ0=sQuery(id+"F0.wireOp",EDGE,"E0.bottom");var subQ1=sQuery(id+"F0.wireOp",EDGE,"E0.top");var subQ2=sQuery(id+"F0.wireOp",EDGE,"E0.left");var subQ3=sQuery(id+"F0.wireOp",EDGE,"E0.right");var subQ4=sQuery(id+"F6.wireOp",EDGE,"E22");var subQ5=sQuery(id+"F6.wireOp",EDGE,"E23.MirrorCS");Q20=makeQuery(id+"F17.boolean.opBoolean","INTERSECT",EDGE,{"disambiguationData":[OD(0.0)],"derivedFrom":[makeQuery(id+"F14.opExtrude","SWEPT_FACE",FACE,{"disambiguationData":[OSD([subQ0,subQ1,subQ2,subQ3,subQ4,subQ5]),TDD([makeQuery(id+"F7.boolean.opBoolean","INTERSECT",EDGE,{"disambiguationData":[OD(0.0)],"derivedFrom":[makeQuery(id+"F1.opExtrude","CAP_FACE",FACE,{"disambiguationData":[OSD([subQ0,subQ1,subQ2,subQ3])],"isStart":false}),makeQuery(id+"F7.opRevolve","SWEPT_FACE",FACE,{"disambiguationData":[OSD([subQ4,subQ5])]})]})])]}),makeQuery(id+"F17.opLoft","SWEPT_FACE",FACE,{"disambiguationData":[OSD([sQuery(id+"F15.wireOp",EDGE,"E46"),sQuery(id+"F16.wireOp",EDGE,"E47")])]})]});}
            var Q21;
            Q21=makeQuery(id+"F17.boolean.opBoolean","INTERSECT",EDGE,{"derivedFrom":[makeQuery(id+"F11.boolean.opBoolean","COPY",FACE,{"derivedFrom":makeQuery(id+"F11.opRevolve","SWEPT_FACE",FACE,{"disambiguationData":[OSD([sQuery(id+"F10.wireOp",EDGE,"E40"),sQuery(id+"F10.wireOp",EDGE,"E41.MirrorCS")])]})}),makeQuery(id+"F17.opLoft","SWEPT_FACE",FACE,{"disambiguationData":[OSD([sQuery(id+"F15.wireOp",EDGE,"E46"),sQuery(id+"F16.wireOp",EDGE,"E47")])]})]});
            var Q22;
            {var subQ0=sQuery(id+"F0.wireOp",EDGE,"E0.bottom");var subQ1=sQuery(id+"F0.wireOp",EDGE,"E0.top");var subQ2=sQuery(id+"F0.wireOp",EDGE,"E0.left");var subQ3=sQuery(id+"F0.wireOp",EDGE,"E0.right");var subQ4=sQuery(id+"F10.wireOp",EDGE,"E40");var subQ5=sQuery(id+"F10.wireOp",EDGE,"E41.MirrorCS");Q22=makeQuery(id+"F17.boolean.opBoolean","INTERSECT",EDGE,{"disambiguationData":[OD(0.0)],"derivedFrom":[makeQuery(id+"F14.opExtrude","SWEPT_FACE",FACE,{"disambiguationData":[OSD([subQ0,subQ1,subQ2,subQ3,subQ4,subQ5]),TDD([makeQuery(id+"F11.boolean.opBoolean","INTERSECT",EDGE,{"disambiguationData":[OD(0.0)],"derivedFrom":[makeQuery(id+"F1.opExtrude","CAP_FACE",FACE,{"disambiguationData":[OSD([subQ0,subQ1,subQ2,subQ3])],"isStart":false}),makeQuery(id+"F11.opRevolve","SWEPT_FACE",FACE,{"disambiguationData":[OSD([subQ4,subQ5])]})]})])]}),makeQuery(id+"F17.opLoft","SWEPT_FACE",FACE,{"disambiguationData":[OSD([sQuery(id+"F15.wireOp",EDGE,"E46"),sQuery(id+"F16.wireOp",EDGE,"E47")])]})]});}
            var Q23;
            {var subQ0=sQuery(id+"F0.wireOp",EDGE,"E0.bottom");var subQ1=sQuery(id+"F0.wireOp",EDGE,"E0.top");var subQ2=sQuery(id+"F0.wireOp",EDGE,"E0.left");var subQ3=sQuery(id+"F0.wireOp",EDGE,"E0.right");var subQ4=sQuery(id+"F10.wireOp",EDGE,"E40");var subQ5=sQuery(id+"F10.wireOp",EDGE,"E41.MirrorCS");Q23=makeQuery(id+"F17.boolean.opBoolean","INTERSECT",EDGE,{"disambiguationData":[OD(1.0)],"derivedFrom":[makeQuery(id+"F14.opExtrude","SWEPT_FACE",FACE,{"disambiguationData":[OSD([subQ0,subQ1,subQ2,subQ3,subQ4,subQ5]),TDD([makeQuery(id+"F11.boolean.opBoolean","INTERSECT",EDGE,{"disambiguationData":[OD(0.0)],"derivedFrom":[makeQuery(id+"F1.opExtrude","CAP_FACE",FACE,{"disambiguationData":[OSD([subQ0,subQ1,subQ2,subQ3])],"isStart":false}),makeQuery(id+"F11.opRevolve","SWEPT_FACE",FACE,{"disambiguationData":[OSD([subQ4,subQ5])]})]})])]}),makeQuery(id+"F17.opLoft","SWEPT_FACE",FACE,{"disambiguationData":[OSD([sQuery(id+"F15.wireOp",EDGE,"E46"),sQuery(id+"F16.wireOp",EDGE,"E47")])]})]});}
            var Q24;
            {var subQ0=sQuery(id+"F0.wireOp",EDGE,"E0.bottom");var subQ1=sQuery(id+"F0.wireOp",EDGE,"E0.top");var subQ2=sQuery(id+"F0.wireOp",EDGE,"E0.left");var subQ3=sQuery(id+"F0.wireOp",EDGE,"E0.right");var subQ4=sQuery(id+"F4.wireOp",EDGE,"E12");var subQ5=sQuery(id+"F4.wireOp",EDGE,"E13");var subQ6=sQuery(id+"F4.wireOp",EDGE,"E14.MirrorCS");Q24=makeQuery(id+"F14.opExtrude","SWEPT_EDGE",EDGE,{"disambiguationData":[OSD([subQ0,subQ1,subQ2,subQ3,subQ4,subQ5,subQ6]),TDD([makeQuery(id+"F5.boolean.opBoolean","INTERSECT",VERTEX,{"disambiguationData":[OD(1.0)],"derivedFrom":[makeQuery(id+"F1.opExtrude","CAP_FACE",FACE,{"disambiguationData":[OSD([subQ0,subQ1,subQ2,subQ3])],"isStart":false}),makeQuery(id+"F5.opRevolve","SWEPT_FACE",FACE,{"disambiguationData":[OSD([subQ4])]}),makeQuery(id+"F5.opRevolve","SWEPT_FACE",FACE,{"disambiguationData":[OSD([subQ5,subQ6])]})]})])]});}
            var Q25;
            {var subQ0=sQuery(id+"F0.wireOp",EDGE,"E0.bottom");var subQ1=sQuery(id+"F0.wireOp",EDGE,"E0.top");var subQ2=sQuery(id+"F0.wireOp",EDGE,"E0.left");var subQ3=sQuery(id+"F0.wireOp",EDGE,"E0.right");var subQ4=sQuery(id+"F4.wireOp",EDGE,"E11");var subQ5=sQuery(id+"F4.wireOp",EDGE,"E12");Q25=makeQuery(id+"F14.opExtrude","SWEPT_EDGE",EDGE,{"disambiguationData":[OSD([subQ0,subQ1,subQ2,subQ3,subQ4,subQ5]),TDD([makeQuery(id+"F5.boolean.opBoolean","INTERSECT",VERTEX,{"disambiguationData":[OD(1.0)],"derivedFrom":[makeQuery(id+"F1.opExtrude","CAP_FACE",FACE,{"disambiguationData":[OSD([subQ0,subQ1,subQ2,subQ3])],"isStart":false}),makeQuery(id+"F5.opRevolve","SWEPT_FACE",FACE,{"disambiguationData":[OSD([subQ4])]}),makeQuery(id+"F5.opRevolve","SWEPT_FACE",FACE,{"disambiguationData":[OSD([subQ5])]})]})])]});}
            var Q26;
            {var subQ0=sQuery(id+"F0.wireOp",EDGE,"E0.bottom");var subQ1=sQuery(id+"F0.wireOp",EDGE,"E0.top");var subQ2=sQuery(id+"F0.wireOp",EDGE,"E0.left");var subQ3=sQuery(id+"F0.wireOp",EDGE,"E0.right");var subQ4=sQuery(id+"F4.wireOp",EDGE,"E10");var subQ5=sQuery(id+"F4.wireOp",EDGE,"E11");Q26=makeQuery(id+"F14.opExtrude","SWEPT_EDGE",EDGE,{"disambiguationData":[OSD([subQ0,subQ1,subQ2,subQ3,subQ4,subQ5]),TDD([makeQuery(id+"F5.boolean.opBoolean","INTERSECT",VERTEX,{"disambiguationData":[OD(1.0)],"derivedFrom":[makeQuery(id+"F1.opExtrude","CAP_FACE",FACE,{"disambiguationData":[OSD([subQ0,subQ1,subQ2,subQ3])],"isStart":false}),makeQuery(id+"F5.opRevolve","SWEPT_FACE",FACE,{"disambiguationData":[OSD([subQ4])]}),makeQuery(id+"F5.opRevolve","SWEPT_FACE",FACE,{"disambiguationData":[OSD([subQ5])]})]})])]});}
            var Q27;
            {var subQ0=sQuery(id+"F0.wireOp",EDGE,"E0.bottom");var subQ1=sQuery(id+"F0.wireOp",EDGE,"E0.top");var subQ2=sQuery(id+"F0.wireOp",EDGE,"E0.left");var subQ3=sQuery(id+"F0.wireOp",EDGE,"E0.right");var subQ4=sQuery(id+"F4.wireOp",EDGE,"E10");var subQ5=sQuery(id+"F4.wireOp",EDGE,"E11");Q27=makeQuery(id+"F14.opExtrude","SWEPT_EDGE",EDGE,{"disambiguationData":[OSD([subQ0,subQ1,subQ2,subQ3,subQ4,subQ5]),TDD([makeQuery(id+"F5.boolean.opBoolean","INTERSECT",VERTEX,{"disambiguationData":[OD(0.0)],"derivedFrom":[makeQuery(id+"F1.opExtrude","CAP_FACE",FACE,{"disambiguationData":[OSD([subQ0,subQ1,subQ2,subQ3])],"isStart":false}),makeQuery(id+"F5.opRevolve","SWEPT_FACE",FACE,{"disambiguationData":[OSD([subQ4])]}),makeQuery(id+"F5.opRevolve","SWEPT_FACE",FACE,{"disambiguationData":[OSD([subQ5])]})]})])]});}
            var Q28;
            {var subQ0=sQuery(id+"F0.wireOp",EDGE,"E0.bottom");var subQ1=sQuery(id+"F0.wireOp",EDGE,"E0.top");var subQ2=sQuery(id+"F0.wireOp",EDGE,"E0.left");var subQ3=sQuery(id+"F0.wireOp",EDGE,"E0.right");var subQ4=sQuery(id+"F4.wireOp",EDGE,"E11");var subQ5=sQuery(id+"F4.wireOp",EDGE,"E12");Q28=makeQuery(id+"F14.opExtrude","SWEPT_EDGE",EDGE,{"disambiguationData":[OSD([subQ0,subQ1,subQ2,subQ3,subQ4,subQ5]),TDD([makeQuery(id+"F5.boolean.opBoolean","INTERSECT",VERTEX,{"disambiguationData":[OD(0.0)],"derivedFrom":[makeQuery(id+"F1.opExtrude","CAP_FACE",FACE,{"disambiguationData":[OSD([subQ0,subQ1,subQ2,subQ3])],"isStart":false}),makeQuery(id+"F5.opRevolve","SWEPT_FACE",FACE,{"disambiguationData":[OSD([subQ4])]}),makeQuery(id+"F5.opRevolve","SWEPT_FACE",FACE,{"disambiguationData":[OSD([subQ5])]})]})])]});}
            var Q29;
            {var subQ0=sQuery(id+"F0.wireOp",EDGE,"E0.bottom");var subQ1=sQuery(id+"F0.wireOp",EDGE,"E0.top");var subQ2=sQuery(id+"F0.wireOp",EDGE,"E0.left");var subQ3=sQuery(id+"F0.wireOp",EDGE,"E0.right");var subQ4=sQuery(id+"F4.wireOp",EDGE,"E12");var subQ5=sQuery(id+"F4.wireOp",EDGE,"E13");var subQ6=sQuery(id+"F4.wireOp",EDGE,"E14.MirrorCS");Q29=makeQuery(id+"F14.opExtrude","SWEPT_EDGE",EDGE,{"disambiguationData":[OSD([subQ0,subQ1,subQ2,subQ3,subQ4,subQ5,subQ6]),TDD([makeQuery(id+"F5.boolean.opBoolean","INTERSECT",VERTEX,{"disambiguationData":[OD(0.0)],"derivedFrom":[makeQuery(id+"F1.opExtrude","CAP_FACE",FACE,{"disambiguationData":[OSD([subQ0,subQ1,subQ2,subQ3])],"isStart":false}),makeQuery(id+"F5.opRevolve","SWEPT_FACE",FACE,{"disambiguationData":[OSD([subQ4])]}),makeQuery(id+"F5.opRevolve","SWEPT_FACE",FACE,{"disambiguationData":[OSD([subQ5,subQ6])]})]})])]});}
            var Q30;
            {var subQ0=sQuery(id+"F0.wireOp",EDGE,"E0.bottom");var subQ1=sQuery(id+"F0.wireOp",EDGE,"E0.top");var subQ2=sQuery(id+"F0.wireOp",EDGE,"E0.left");var subQ3=sQuery(id+"F0.wireOp",EDGE,"E0.right");var subQ4=sQuery(id+"F6.wireOp",EDGE,"E21");var subQ5=sQuery(id+"F6.wireOp",EDGE,"E22");var subQ6=sQuery(id+"F6.wireOp",EDGE,"E23.MirrorCS");Q30=makeQuery(id+"F14.opExtrude","SWEPT_EDGE",EDGE,{"disambiguationData":[OSD([subQ0,subQ1,subQ2,subQ3,subQ4,subQ5,subQ6]),TDD([makeQuery(id+"F7.boolean.opBoolean","INTERSECT",VERTEX,{"disambiguationData":[OD(1.0)],"derivedFrom":[makeQuery(id+"F1.opExtrude","CAP_FACE",FACE,{"disambiguationData":[OSD([subQ0,subQ1,subQ2,subQ3])],"isStart":false}),makeQuery(id+"F7.opRevolve","SWEPT_FACE",FACE,{"disambiguationData":[OSD([subQ4])]}),makeQuery(id+"F7.opRevolve","SWEPT_FACE",FACE,{"disambiguationData":[OSD([subQ5,subQ6])]})]})])]});}
            var Q31;
            {var subQ0=sQuery(id+"F0.wireOp",EDGE,"E0.bottom");var subQ1=sQuery(id+"F0.wireOp",EDGE,"E0.top");var subQ2=sQuery(id+"F0.wireOp",EDGE,"E0.left");var subQ3=sQuery(id+"F0.wireOp",EDGE,"E0.right");var subQ4=sQuery(id+"F6.wireOp",EDGE,"E20");var subQ5=sQuery(id+"F6.wireOp",EDGE,"E21");Q31=makeQuery(id+"F14.opExtrude","SWEPT_EDGE",EDGE,{"disambiguationData":[OSD([subQ0,subQ1,subQ2,subQ3,subQ4,subQ5]),TDD([makeQuery(id+"F7.boolean.opBoolean","INTERSECT",VERTEX,{"disambiguationData":[OD(1.0)],"derivedFrom":[makeQuery(id+"F1.opExtrude","CAP_FACE",FACE,{"disambiguationData":[OSD([subQ0,subQ1,subQ2,subQ3])],"isStart":false}),makeQuery(id+"F7.opRevolve","SWEPT_FACE",FACE,{"disambiguationData":[OSD([subQ4])]}),makeQuery(id+"F7.opRevolve","SWEPT_FACE",FACE,{"disambiguationData":[OSD([subQ5])]})]})])]});}
            var Q32;
            {var subQ0=sQuery(id+"F0.wireOp",EDGE,"E0.bottom");var subQ1=sQuery(id+"F0.wireOp",EDGE,"E0.top");var subQ2=sQuery(id+"F0.wireOp",EDGE,"E0.left");var subQ3=sQuery(id+"F0.wireOp",EDGE,"E0.right");var subQ4=sQuery(id+"F6.wireOp",EDGE,"E19");var subQ5=sQuery(id+"F6.wireOp",EDGE,"E20");Q32=makeQuery(id+"F14.opExtrude","SWEPT_EDGE",EDGE,{"disambiguationData":[OSD([subQ0,subQ1,subQ2,subQ3,subQ4,subQ5]),TDD([makeQuery(id+"F7.boolean.opBoolean","INTERSECT",VERTEX,{"disambiguationData":[OD(1.0)],"derivedFrom":[makeQuery(id+"F1.opExtrude","CAP_FACE",FACE,{"disambiguationData":[OSD([subQ0,subQ1,subQ2,subQ3])],"isStart":false}),makeQuery(id+"F7.opRevolve","SWEPT_FACE",FACE,{"disambiguationData":[OSD([subQ4])]}),makeQuery(id+"F7.opRevolve","SWEPT_FACE",FACE,{"disambiguationData":[OSD([subQ5])]})]})])]});}
            var Q33;
            {var subQ0=sQuery(id+"F0.wireOp",EDGE,"E0.bottom");var subQ1=sQuery(id+"F0.wireOp",EDGE,"E0.top");var subQ2=sQuery(id+"F0.wireOp",EDGE,"E0.left");var subQ3=sQuery(id+"F0.wireOp",EDGE,"E0.right");var subQ4=sQuery(id+"F6.wireOp",EDGE,"E19");var subQ5=sQuery(id+"F6.wireOp",EDGE,"E20");Q33=makeQuery(id+"F14.opExtrude","SWEPT_EDGE",EDGE,{"disambiguationData":[OSD([subQ0,subQ1,subQ2,subQ3,subQ4,subQ5]),TDD([makeQuery(id+"F7.boolean.opBoolean","INTERSECT",VERTEX,{"disambiguationData":[OD(0.0)],"derivedFrom":[makeQuery(id+"F1.opExtrude","CAP_FACE",FACE,{"disambiguationData":[OSD([subQ0,subQ1,subQ2,subQ3])],"isStart":false}),makeQuery(id+"F7.opRevolve","SWEPT_FACE",FACE,{"disambiguationData":[OSD([subQ4])]}),makeQuery(id+"F7.opRevolve","SWEPT_FACE",FACE,{"disambiguationData":[OSD([subQ5])]})]})])]});}
            var Q34;
            {var subQ0=sQuery(id+"F0.wireOp",EDGE,"E0.bottom");var subQ1=sQuery(id+"F0.wireOp",EDGE,"E0.top");var subQ2=sQuery(id+"F0.wireOp",EDGE,"E0.left");var subQ3=sQuery(id+"F0.wireOp",EDGE,"E0.right");var subQ4=sQuery(id+"F6.wireOp",EDGE,"E20");var subQ5=sQuery(id+"F6.wireOp",EDGE,"E21");Q34=makeQuery(id+"F14.opExtrude","SWEPT_EDGE",EDGE,{"disambiguationData":[OSD([subQ0,subQ1,subQ2,subQ3,subQ4,subQ5]),TDD([makeQuery(id+"F7.boolean.opBoolean","INTERSECT",VERTEX,{"disambiguationData":[OD(0.0)],"derivedFrom":[makeQuery(id+"F1.opExtrude","CAP_FACE",FACE,{"disambiguationData":[OSD([subQ0,subQ1,subQ2,subQ3])],"isStart":false}),makeQuery(id+"F7.opRevolve","SWEPT_FACE",FACE,{"disambiguationData":[OSD([subQ4])]}),makeQuery(id+"F7.opRevolve","SWEPT_FACE",FACE,{"disambiguationData":[OSD([subQ5])]})]})])]});}
            var Q35;
            {var subQ0=sQuery(id+"F0.wireOp",EDGE,"E0.bottom");var subQ1=sQuery(id+"F0.wireOp",EDGE,"E0.top");var subQ2=sQuery(id+"F0.wireOp",EDGE,"E0.left");var subQ3=sQuery(id+"F0.wireOp",EDGE,"E0.right");var subQ4=sQuery(id+"F6.wireOp",EDGE,"E21");var subQ5=sQuery(id+"F6.wireOp",EDGE,"E22");var subQ6=sQuery(id+"F6.wireOp",EDGE,"E23.MirrorCS");Q35=makeQuery(id+"F14.opExtrude","SWEPT_EDGE",EDGE,{"disambiguationData":[OSD([subQ0,subQ1,subQ2,subQ3,subQ4,subQ5,subQ6]),TDD([makeQuery(id+"F7.boolean.opBoolean","INTERSECT",VERTEX,{"disambiguationData":[OD(0.0)],"derivedFrom":[makeQuery(id+"F1.opExtrude","CAP_FACE",FACE,{"disambiguationData":[OSD([subQ0,subQ1,subQ2,subQ3])],"isStart":false}),makeQuery(id+"F7.opRevolve","SWEPT_FACE",FACE,{"disambiguationData":[OSD([subQ4])]}),makeQuery(id+"F7.opRevolve","SWEPT_FACE",FACE,{"disambiguationData":[OSD([subQ5,subQ6])]})]})])]});}
            var Q36;
            {var subQ0=sQuery(id+"F0.wireOp",EDGE,"E0.bottom");var subQ1=sQuery(id+"F0.wireOp",EDGE,"E0.top");var subQ2=sQuery(id+"F0.wireOp",EDGE,"E0.left");var subQ3=sQuery(id+"F0.wireOp",EDGE,"E0.right");var subQ4=sQuery(id+"F2.wireOp",EDGE,"E3");var subQ5=sQuery(id+"F2.wireOp",EDGE,"E4");var subQ6=sQuery(id+"F2.wireOp",EDGE,"E5.MirrorCS");Q36=makeQuery(id+"F14.opExtrude","SWEPT_EDGE",EDGE,{"disambiguationData":[OSD([subQ0,subQ1,subQ2,subQ3,subQ4,subQ5,subQ6]),TDD([makeQuery(id+"F3.boolean.opBoolean","INTERSECT",VERTEX,{"disambiguationData":[OD(1.0)],"derivedFrom":[makeQuery(id+"F1.opExtrude","CAP_FACE",FACE,{"disambiguationData":[OSD([subQ0,subQ1,subQ2,subQ3])],"isStart":false}),makeQuery(id+"F3.opRevolve","SWEPT_FACE",FACE,{"disambiguationData":[OSD([subQ4])]}),makeQuery(id+"F3.opRevolve","SWEPT_FACE",FACE,{"disambiguationData":[OSD([subQ5,subQ6])]})]})])]});}
            var Q37;
            {var subQ0=sQuery(id+"F0.wireOp",EDGE,"E0.bottom");var subQ1=sQuery(id+"F0.wireOp",EDGE,"E0.top");var subQ2=sQuery(id+"F0.wireOp",EDGE,"E0.left");var subQ3=sQuery(id+"F0.wireOp",EDGE,"E0.right");var subQ4=sQuery(id+"F2.wireOp",EDGE,"E2");var subQ5=sQuery(id+"F2.wireOp",EDGE,"E3");Q37=makeQuery(id+"F14.opExtrude","SWEPT_EDGE",EDGE,{"disambiguationData":[OSD([subQ0,subQ1,subQ2,subQ3,subQ4,subQ5]),TDD([makeQuery(id+"F3.boolean.opBoolean","INTERSECT",VERTEX,{"disambiguationData":[OD(1.0)],"derivedFrom":[makeQuery(id+"F1.opExtrude","CAP_FACE",FACE,{"disambiguationData":[OSD([subQ0,subQ1,subQ2,subQ3])],"isStart":false}),makeQuery(id+"F3.opRevolve","SWEPT_FACE",FACE,{"disambiguationData":[OSD([subQ4])]}),makeQuery(id+"F3.opRevolve","SWEPT_FACE",FACE,{"disambiguationData":[OSD([subQ5])]})]})])]});}
            var Q38;
            {var subQ0=sQuery(id+"F0.wireOp",EDGE,"E0.bottom");var subQ1=sQuery(id+"F0.wireOp",EDGE,"E0.top");var subQ2=sQuery(id+"F0.wireOp",EDGE,"E0.left");var subQ3=sQuery(id+"F0.wireOp",EDGE,"E0.right");var subQ4=sQuery(id+"F2.wireOp",EDGE,"E1");var subQ5=sQuery(id+"F2.wireOp",EDGE,"E2");Q38=makeQuery(id+"F14.opExtrude","SWEPT_EDGE",EDGE,{"disambiguationData":[OSD([subQ0,subQ1,subQ2,subQ3,subQ4,subQ5]),TDD([makeQuery(id+"F3.boolean.opBoolean","INTERSECT",VERTEX,{"disambiguationData":[OD(1.0)],"derivedFrom":[makeQuery(id+"F1.opExtrude","CAP_FACE",FACE,{"disambiguationData":[OSD([subQ0,subQ1,subQ2,subQ3])],"isStart":false}),makeQuery(id+"F3.opRevolve","SWEPT_FACE",FACE,{"disambiguationData":[OSD([subQ4])]}),makeQuery(id+"F3.opRevolve","SWEPT_FACE",FACE,{"disambiguationData":[OSD([subQ5])]})]})])]});}
            var Q39;
            {var subQ0=sQuery(id+"F0.wireOp",EDGE,"E0.bottom");var subQ1=sQuery(id+"F0.wireOp",EDGE,"E0.top");var subQ2=sQuery(id+"F0.wireOp",EDGE,"E0.left");var subQ3=sQuery(id+"F0.wireOp",EDGE,"E0.right");var subQ4=sQuery(id+"F2.wireOp",EDGE,"E1");var subQ5=sQuery(id+"F2.wireOp",EDGE,"E2");Q39=makeQuery(id+"F14.opExtrude","SWEPT_EDGE",EDGE,{"disambiguationData":[OSD([subQ0,subQ1,subQ2,subQ3,subQ4,subQ5]),TDD([makeQuery(id+"F3.boolean.opBoolean","INTERSECT",VERTEX,{"disambiguationData":[OD(0.0)],"derivedFrom":[makeQuery(id+"F1.opExtrude","CAP_FACE",FACE,{"disambiguationData":[OSD([subQ0,subQ1,subQ2,subQ3])],"isStart":false}),makeQuery(id+"F3.opRevolve","SWEPT_FACE",FACE,{"disambiguationData":[OSD([subQ4])]}),makeQuery(id+"F3.opRevolve","SWEPT_FACE",FACE,{"disambiguationData":[OSD([subQ5])]})]})])]});}
            var Q40;
            {var subQ0=sQuery(id+"F0.wireOp",EDGE,"E0.bottom");var subQ1=sQuery(id+"F0.wireOp",EDGE,"E0.top");var subQ2=sQuery(id+"F0.wireOp",EDGE,"E0.left");var subQ3=sQuery(id+"F0.wireOp",EDGE,"E0.right");var subQ4=sQuery(id+"F2.wireOp",EDGE,"E2");var subQ5=sQuery(id+"F2.wireOp",EDGE,"E3");Q40=makeQuery(id+"F14.opExtrude","SWEPT_EDGE",EDGE,{"disambiguationData":[OSD([subQ0,subQ1,subQ2,subQ3,subQ4,subQ5]),TDD([makeQuery(id+"F3.boolean.opBoolean","INTERSECT",VERTEX,{"disambiguationData":[OD(0.0)],"derivedFrom":[makeQuery(id+"F1.opExtrude","CAP_FACE",FACE,{"disambiguationData":[OSD([subQ0,subQ1,subQ2,subQ3])],"isStart":false}),makeQuery(id+"F3.opRevolve","SWEPT_FACE",FACE,{"disambiguationData":[OSD([subQ4])]}),makeQuery(id+"F3.opRevolve","SWEPT_FACE",FACE,{"disambiguationData":[OSD([subQ5])]})]})])]});}
            var Q41;
            {var subQ0=sQuery(id+"F0.wireOp",EDGE,"E0.bottom");var subQ1=sQuery(id+"F0.wireOp",EDGE,"E0.top");var subQ2=sQuery(id+"F0.wireOp",EDGE,"E0.left");var subQ3=sQuery(id+"F0.wireOp",EDGE,"E0.right");var subQ4=sQuery(id+"F2.wireOp",EDGE,"E3");var subQ5=sQuery(id+"F2.wireOp",EDGE,"E4");var subQ6=sQuery(id+"F2.wireOp",EDGE,"E5.MirrorCS");Q41=makeQuery(id+"F14.opExtrude","SWEPT_EDGE",EDGE,{"disambiguationData":[OSD([subQ0,subQ1,subQ2,subQ3,subQ4,subQ5,subQ6]),TDD([makeQuery(id+"F3.boolean.opBoolean","INTERSECT",VERTEX,{"disambiguationData":[OD(0.0)],"derivedFrom":[makeQuery(id+"F1.opExtrude","CAP_FACE",FACE,{"disambiguationData":[OSD([subQ0,subQ1,subQ2,subQ3])],"isStart":false}),makeQuery(id+"F3.opRevolve","SWEPT_FACE",FACE,{"disambiguationData":[OSD([subQ4])]}),makeQuery(id+"F3.opRevolve","SWEPT_FACE",FACE,{"disambiguationData":[OSD([subQ5,subQ6])]})]})])]});}
            var Q42;
            {var subQ0=sQuery(id+"F0.wireOp",EDGE,"E0.bottom");var subQ1=sQuery(id+"F0.wireOp",EDGE,"E0.top");var subQ2=sQuery(id+"F0.wireOp",EDGE,"E0.left");var subQ3=sQuery(id+"F0.wireOp",EDGE,"E0.right");var subQ4=sQuery(id+"F2.wireOp",EDGE,"E4");var subQ5=sQuery(id+"F2.wireOp",EDGE,"E5.MirrorCS");var subQ6=sQuery(id+"F2.wireOp",EDGE,"E6.MirrorCS");Q42=makeQuery(id+"F14.opExtrude","SWEPT_EDGE",EDGE,{"disambiguationData":[OSD([subQ0,subQ1,subQ2,subQ3,subQ4,subQ5,subQ6]),TDD([makeQuery(id+"F3.boolean.opBoolean","INTERSECT",VERTEX,{"disambiguationData":[OD(0.0)],"derivedFrom":[makeQuery(id+"F1.opExtrude","CAP_FACE",FACE,{"disambiguationData":[OSD([subQ0,subQ1,subQ2,subQ3])],"isStart":false}),makeQuery(id+"F3.opRevolve","SWEPT_FACE",FACE,{"disambiguationData":[OSD([subQ4,subQ5])]}),makeQuery(id+"F3.opRevolve","SWEPT_FACE",FACE,{"disambiguationData":[OSD([subQ6])]})]})])]});}
            var Q43;
            {var subQ0=sQuery(id+"F0.wireOp",EDGE,"E0.bottom");var subQ1=sQuery(id+"F0.wireOp",EDGE,"E0.top");var subQ2=sQuery(id+"F0.wireOp",EDGE,"E0.left");var subQ3=sQuery(id+"F0.wireOp",EDGE,"E0.right");var subQ4=sQuery(id+"F2.wireOp",EDGE,"E6.MirrorCS");var subQ5=sQuery(id+"F2.wireOp",EDGE,"E8.MirrorCS");Q43=makeQuery(id+"F14.opExtrude","SWEPT_EDGE",EDGE,{"disambiguationData":[OSD([subQ0,subQ1,subQ2,subQ3,subQ4,subQ5]),TDD([makeQuery(id+"F3.boolean.opBoolean","INTERSECT",VERTEX,{"disambiguationData":[OD(0.0)],"derivedFrom":[makeQuery(id+"F1.opExtrude","CAP_FACE",FACE,{"disambiguationData":[OSD([subQ0,subQ1,subQ2,subQ3])],"isStart":false}),makeQuery(id+"F3.opRevolve","SWEPT_FACE",FACE,{"disambiguationData":[OSD([subQ4])]}),makeQuery(id+"F3.opRevolve","SWEPT_FACE",FACE,{"disambiguationData":[OSD([subQ5])]})]})])]});}
            var Q44;
            {var subQ0=sQuery(id+"F0.wireOp",EDGE,"E0.bottom");var subQ1=sQuery(id+"F0.wireOp",EDGE,"E0.top");var subQ2=sQuery(id+"F0.wireOp",EDGE,"E0.left");var subQ3=sQuery(id+"F0.wireOp",EDGE,"E0.right");var subQ4=sQuery(id+"F2.wireOp",EDGE,"E7.MirrorCS");var subQ5=sQuery(id+"F2.wireOp",EDGE,"E8.MirrorCS");Q44=makeQuery(id+"F14.opExtrude","SWEPT_EDGE",EDGE,{"disambiguationData":[OSD([subQ0,subQ1,subQ2,subQ3,subQ4,subQ5]),TDD([makeQuery(id+"F3.boolean.opBoolean","INTERSECT",VERTEX,{"disambiguationData":[OD(0.0)],"derivedFrom":[makeQuery(id+"F1.opExtrude","CAP_FACE",FACE,{"disambiguationData":[OSD([subQ0,subQ1,subQ2,subQ3])],"isStart":false}),makeQuery(id+"F3.opRevolve","SWEPT_FACE",FACE,{"disambiguationData":[OSD([subQ4])]}),makeQuery(id+"F3.opRevolve","SWEPT_FACE",FACE,{"disambiguationData":[OSD([subQ5])]})]})])]});}
            var Q45;
            {var subQ0=sQuery(id+"F0.wireOp",EDGE,"E0.bottom");var subQ1=sQuery(id+"F0.wireOp",EDGE,"E0.top");var subQ2=sQuery(id+"F0.wireOp",EDGE,"E0.left");var subQ3=sQuery(id+"F0.wireOp",EDGE,"E0.right");var subQ4=sQuery(id+"F2.wireOp",EDGE,"E7.MirrorCS");var subQ5=sQuery(id+"F2.wireOp",EDGE,"E8.MirrorCS");Q45=makeQuery(id+"F14.opExtrude","SWEPT_EDGE",EDGE,{"disambiguationData":[OSD([subQ0,subQ1,subQ2,subQ3,subQ4,subQ5]),TDD([makeQuery(id+"F3.boolean.opBoolean","INTERSECT",VERTEX,{"disambiguationData":[OD(1.0)],"derivedFrom":[makeQuery(id+"F1.opExtrude","CAP_FACE",FACE,{"disambiguationData":[OSD([subQ0,subQ1,subQ2,subQ3])],"isStart":false}),makeQuery(id+"F3.opRevolve","SWEPT_FACE",FACE,{"disambiguationData":[OSD([subQ4])]}),makeQuery(id+"F3.opRevolve","SWEPT_FACE",FACE,{"disambiguationData":[OSD([subQ5])]})]})])]});}
            var Q46;
            {var subQ0=sQuery(id+"F0.wireOp",EDGE,"E0.bottom");var subQ1=sQuery(id+"F0.wireOp",EDGE,"E0.top");var subQ2=sQuery(id+"F0.wireOp",EDGE,"E0.left");var subQ3=sQuery(id+"F0.wireOp",EDGE,"E0.right");var subQ4=sQuery(id+"F2.wireOp",EDGE,"E6.MirrorCS");var subQ5=sQuery(id+"F2.wireOp",EDGE,"E8.MirrorCS");Q46=makeQuery(id+"F14.opExtrude","SWEPT_EDGE",EDGE,{"disambiguationData":[OSD([subQ0,subQ1,subQ2,subQ3,subQ4,subQ5]),TDD([makeQuery(id+"F3.boolean.opBoolean","INTERSECT",VERTEX,{"disambiguationData":[OD(1.0)],"derivedFrom":[makeQuery(id+"F1.opExtrude","CAP_FACE",FACE,{"disambiguationData":[OSD([subQ0,subQ1,subQ2,subQ3])],"isStart":false}),makeQuery(id+"F3.opRevolve","SWEPT_FACE",FACE,{"disambiguationData":[OSD([subQ4])]}),makeQuery(id+"F3.opRevolve","SWEPT_FACE",FACE,{"disambiguationData":[OSD([subQ5])]})]})])]});}
            var Q47;
            {var subQ0=sQuery(id+"F0.wireOp",EDGE,"E0.bottom");var subQ1=sQuery(id+"F0.wireOp",EDGE,"E0.top");var subQ2=sQuery(id+"F0.wireOp",EDGE,"E0.left");var subQ3=sQuery(id+"F0.wireOp",EDGE,"E0.right");var subQ4=sQuery(id+"F2.wireOp",EDGE,"E4");var subQ5=sQuery(id+"F2.wireOp",EDGE,"E5.MirrorCS");var subQ6=sQuery(id+"F2.wireOp",EDGE,"E6.MirrorCS");Q47=makeQuery(id+"F14.opExtrude","SWEPT_EDGE",EDGE,{"disambiguationData":[OSD([subQ0,subQ1,subQ2,subQ3,subQ4,subQ5,subQ6]),TDD([makeQuery(id+"F3.boolean.opBoolean","INTERSECT",VERTEX,{"disambiguationData":[OD(1.0)],"derivedFrom":[makeQuery(id+"F1.opExtrude","CAP_FACE",FACE,{"disambiguationData":[OSD([subQ0,subQ1,subQ2,subQ3])],"isStart":false}),makeQuery(id+"F3.opRevolve","SWEPT_FACE",FACE,{"disambiguationData":[OSD([subQ4,subQ5])]}),makeQuery(id+"F3.opRevolve","SWEPT_FACE",FACE,{"disambiguationData":[OSD([subQ6])]})]})])]});}
            var Q48;
            {var subQ0=sQuery(id+"F0.wireOp",EDGE,"E0.bottom");var subQ1=sQuery(id+"F0.wireOp",EDGE,"E0.top");var subQ2=sQuery(id+"F0.wireOp",EDGE,"E0.left");var subQ3=sQuery(id+"F0.wireOp",EDGE,"E0.right");var subQ4=sQuery(id+"F4.wireOp",EDGE,"E13");var subQ5=sQuery(id+"F4.wireOp",EDGE,"E14.MirrorCS");var subQ6=sQuery(id+"F4.wireOp",EDGE,"E15.MirrorCS");Q48=makeQuery(id+"F14.opExtrude","SWEPT_EDGE",EDGE,{"disambiguationData":[OSD([subQ0,subQ1,subQ2,subQ3,subQ4,subQ5,subQ6]),TDD([makeQuery(id+"F5.boolean.opBoolean","INTERSECT",VERTEX,{"disambiguationData":[OD(1.0)],"derivedFrom":[makeQuery(id+"F1.opExtrude","CAP_FACE",FACE,{"disambiguationData":[OSD([subQ0,subQ1,subQ2,subQ3])],"isStart":false}),makeQuery(id+"F5.opRevolve","SWEPT_FACE",FACE,{"disambiguationData":[OSD([subQ4,subQ5])]}),makeQuery(id+"F5.opRevolve","SWEPT_FACE",FACE,{"disambiguationData":[OSD([subQ6])]})]})])]});}
            var Q49;
            {var subQ0=sQuery(id+"F0.wireOp",EDGE,"E0.bottom");var subQ1=sQuery(id+"F0.wireOp",EDGE,"E0.top");var subQ2=sQuery(id+"F0.wireOp",EDGE,"E0.left");var subQ3=sQuery(id+"F0.wireOp",EDGE,"E0.right");var subQ4=sQuery(id+"F4.wireOp",EDGE,"E15.MirrorCS");var subQ5=sQuery(id+"F4.wireOp",EDGE,"E17.MirrorCS");Q49=makeQuery(id+"F14.opExtrude","SWEPT_EDGE",EDGE,{"disambiguationData":[OSD([subQ0,subQ1,subQ2,subQ3,subQ4,subQ5]),TDD([makeQuery(id+"F5.boolean.opBoolean","INTERSECT",VERTEX,{"disambiguationData":[OD(1.0)],"derivedFrom":[makeQuery(id+"F1.opExtrude","CAP_FACE",FACE,{"disambiguationData":[OSD([subQ0,subQ1,subQ2,subQ3])],"isStart":false}),makeQuery(id+"F5.opRevolve","SWEPT_FACE",FACE,{"disambiguationData":[OSD([subQ4])]}),makeQuery(id+"F5.opRevolve","SWEPT_FACE",FACE,{"disambiguationData":[OSD([subQ5])]})]})])]});}
            var Q50;
            {var subQ0=sQuery(id+"F0.wireOp",EDGE,"E0.bottom");var subQ1=sQuery(id+"F0.wireOp",EDGE,"E0.top");var subQ2=sQuery(id+"F0.wireOp",EDGE,"E0.left");var subQ3=sQuery(id+"F0.wireOp",EDGE,"E0.right");var subQ4=sQuery(id+"F4.wireOp",EDGE,"E16.MirrorCS");var subQ5=sQuery(id+"F4.wireOp",EDGE,"E17.MirrorCS");Q50=makeQuery(id+"F14.opExtrude","SWEPT_EDGE",EDGE,{"disambiguationData":[OSD([subQ0,subQ1,subQ2,subQ3,subQ4,subQ5]),TDD([makeQuery(id+"F5.boolean.opBoolean","INTERSECT",VERTEX,{"disambiguationData":[OD(1.0)],"derivedFrom":[makeQuery(id+"F1.opExtrude","CAP_FACE",FACE,{"disambiguationData":[OSD([subQ0,subQ1,subQ2,subQ3])],"isStart":false}),makeQuery(id+"F5.opRevolve","SWEPT_FACE",FACE,{"disambiguationData":[OSD([subQ4])]}),makeQuery(id+"F5.opRevolve","SWEPT_FACE",FACE,{"disambiguationData":[OSD([subQ5])]})]})])]});}
            var Q51;
            {var subQ0=sQuery(id+"F0.wireOp",EDGE,"E0.bottom");var subQ1=sQuery(id+"F0.wireOp",EDGE,"E0.top");var subQ2=sQuery(id+"F0.wireOp",EDGE,"E0.left");var subQ3=sQuery(id+"F0.wireOp",EDGE,"E0.right");var subQ4=sQuery(id+"F6.wireOp",EDGE,"E25.MirrorCS");var subQ5=sQuery(id+"F6.wireOp",EDGE,"E26.MirrorCS");Q51=makeQuery(id+"F14.opExtrude","SWEPT_EDGE",EDGE,{"disambiguationData":[OSD([subQ0,subQ1,subQ2,subQ3,subQ4,subQ5]),TDD([makeQuery(id+"F7.boolean.opBoolean","INTERSECT",VERTEX,{"disambiguationData":[OD(1.0)],"derivedFrom":[makeQuery(id+"F1.opExtrude","CAP_FACE",FACE,{"disambiguationData":[OSD([subQ0,subQ1,subQ2,subQ3])],"isStart":false}),makeQuery(id+"F7.opRevolve","SWEPT_FACE",FACE,{"disambiguationData":[OSD([subQ4])]}),makeQuery(id+"F7.opRevolve","SWEPT_FACE",FACE,{"disambiguationData":[OSD([subQ5])]})]})])]});}
            var Q52;
            {var subQ0=sQuery(id+"F0.wireOp",EDGE,"E0.bottom");var subQ1=sQuery(id+"F0.wireOp",EDGE,"E0.top");var subQ2=sQuery(id+"F0.wireOp",EDGE,"E0.left");var subQ3=sQuery(id+"F0.wireOp",EDGE,"E0.right");var subQ4=sQuery(id+"F6.wireOp",EDGE,"E24.MirrorCS");var subQ5=sQuery(id+"F6.wireOp",EDGE,"E26.MirrorCS");Q52=makeQuery(id+"F14.opExtrude","SWEPT_EDGE",EDGE,{"disambiguationData":[OSD([subQ0,subQ1,subQ2,subQ3,subQ4,subQ5]),TDD([makeQuery(id+"F7.boolean.opBoolean","INTERSECT",VERTEX,{"disambiguationData":[OD(1.0)],"derivedFrom":[makeQuery(id+"F1.opExtrude","CAP_FACE",FACE,{"disambiguationData":[OSD([subQ0,subQ1,subQ2,subQ3])],"isStart":false}),makeQuery(id+"F7.opRevolve","SWEPT_FACE",FACE,{"disambiguationData":[OSD([subQ4])]}),makeQuery(id+"F7.opRevolve","SWEPT_FACE",FACE,{"disambiguationData":[OSD([subQ5])]})]})])]});}
            var Q53;
            {var subQ0=sQuery(id+"F0.wireOp",EDGE,"E0.bottom");var subQ1=sQuery(id+"F0.wireOp",EDGE,"E0.top");var subQ2=sQuery(id+"F0.wireOp",EDGE,"E0.left");var subQ3=sQuery(id+"F0.wireOp",EDGE,"E0.right");var subQ4=sQuery(id+"F6.wireOp",EDGE,"E22");var subQ5=sQuery(id+"F6.wireOp",EDGE,"E23.MirrorCS");var subQ6=sQuery(id+"F6.wireOp",EDGE,"E24.MirrorCS");Q53=makeQuery(id+"F14.opExtrude","SWEPT_EDGE",EDGE,{"disambiguationData":[OSD([subQ0,subQ1,subQ2,subQ3,subQ4,subQ5,subQ6]),TDD([makeQuery(id+"F7.boolean.opBoolean","INTERSECT",VERTEX,{"disambiguationData":[OD(1.0)],"derivedFrom":[makeQuery(id+"F1.opExtrude","CAP_FACE",FACE,{"disambiguationData":[OSD([subQ0,subQ1,subQ2,subQ3])],"isStart":false}),makeQuery(id+"F7.opRevolve","SWEPT_FACE",FACE,{"disambiguationData":[OSD([subQ4,subQ5])]}),makeQuery(id+"F7.opRevolve","SWEPT_FACE",FACE,{"disambiguationData":[OSD([subQ6])]})]})])]});}
            var Q54;
            {var subQ0=sQuery(id+"F0.wireOp",EDGE,"E0.bottom");var subQ1=sQuery(id+"F0.wireOp",EDGE,"E0.top");var subQ2=sQuery(id+"F0.wireOp",EDGE,"E0.left");var subQ3=sQuery(id+"F0.wireOp",EDGE,"E0.right");var subQ4=sQuery(id+"F6.wireOp",EDGE,"E25.MirrorCS");var subQ5=sQuery(id+"F6.wireOp",EDGE,"E26.MirrorCS");Q54=makeQuery(id+"F14.opExtrude","SWEPT_EDGE",EDGE,{"disambiguationData":[OSD([subQ0,subQ1,subQ2,subQ3,subQ4,subQ5]),TDD([makeQuery(id+"F7.boolean.opBoolean","INTERSECT",VERTEX,{"disambiguationData":[OD(0.0)],"derivedFrom":[makeQuery(id+"F1.opExtrude","CAP_FACE",FACE,{"disambiguationData":[OSD([subQ0,subQ1,subQ2,subQ3])],"isStart":false}),makeQuery(id+"F7.opRevolve","SWEPT_FACE",FACE,{"disambiguationData":[OSD([subQ4])]}),makeQuery(id+"F7.opRevolve","SWEPT_FACE",FACE,{"disambiguationData":[OSD([subQ5])]})]})])]});}
            var Q55;
            {var subQ0=sQuery(id+"F0.wireOp",EDGE,"E0.bottom");var subQ1=sQuery(id+"F0.wireOp",EDGE,"E0.top");var subQ2=sQuery(id+"F0.wireOp",EDGE,"E0.left");var subQ3=sQuery(id+"F0.wireOp",EDGE,"E0.right");var subQ4=sQuery(id+"F6.wireOp",EDGE,"E24.MirrorCS");var subQ5=sQuery(id+"F6.wireOp",EDGE,"E26.MirrorCS");Q55=makeQuery(id+"F14.opExtrude","SWEPT_EDGE",EDGE,{"disambiguationData":[OSD([subQ0,subQ1,subQ2,subQ3,subQ4,subQ5]),TDD([makeQuery(id+"F7.boolean.opBoolean","INTERSECT",VERTEX,{"disambiguationData":[OD(0.0)],"derivedFrom":[makeQuery(id+"F1.opExtrude","CAP_FACE",FACE,{"disambiguationData":[OSD([subQ0,subQ1,subQ2,subQ3])],"isStart":false}),makeQuery(id+"F7.opRevolve","SWEPT_FACE",FACE,{"disambiguationData":[OSD([subQ4])]}),makeQuery(id+"F7.opRevolve","SWEPT_FACE",FACE,{"disambiguationData":[OSD([subQ5])]})]})])]});}
            var Q56;
            {var subQ0=sQuery(id+"F0.wireOp",EDGE,"E0.bottom");var subQ1=sQuery(id+"F0.wireOp",EDGE,"E0.top");var subQ2=sQuery(id+"F0.wireOp",EDGE,"E0.left");var subQ3=sQuery(id+"F0.wireOp",EDGE,"E0.right");var subQ4=sQuery(id+"F6.wireOp",EDGE,"E22");var subQ5=sQuery(id+"F6.wireOp",EDGE,"E23.MirrorCS");var subQ6=sQuery(id+"F6.wireOp",EDGE,"E24.MirrorCS");Q56=makeQuery(id+"F14.opExtrude","SWEPT_EDGE",EDGE,{"disambiguationData":[OSD([subQ0,subQ1,subQ2,subQ3,subQ4,subQ5,subQ6]),TDD([makeQuery(id+"F7.boolean.opBoolean","INTERSECT",VERTEX,{"disambiguationData":[OD(0.0)],"derivedFrom":[makeQuery(id+"F1.opExtrude","CAP_FACE",FACE,{"disambiguationData":[OSD([subQ0,subQ1,subQ2,subQ3])],"isStart":false}),makeQuery(id+"F7.opRevolve","SWEPT_FACE",FACE,{"disambiguationData":[OSD([subQ4,subQ5])]}),makeQuery(id+"F7.opRevolve","SWEPT_FACE",FACE,{"disambiguationData":[OSD([subQ6])]})]})])]});}
            var Q57;
            {var subQ0=sQuery(id+"F0.wireOp",EDGE,"E0.bottom");var subQ1=sQuery(id+"F0.wireOp",EDGE,"E0.top");var subQ2=sQuery(id+"F0.wireOp",EDGE,"E0.left");var subQ3=sQuery(id+"F0.wireOp",EDGE,"E0.right");var subQ4=sQuery(id+"F4.wireOp",EDGE,"E13");var subQ5=sQuery(id+"F4.wireOp",EDGE,"E14.MirrorCS");var subQ6=sQuery(id+"F4.wireOp",EDGE,"E15.MirrorCS");Q57=makeQuery(id+"F14.opExtrude","SWEPT_EDGE",EDGE,{"disambiguationData":[OSD([subQ0,subQ1,subQ2,subQ3,subQ4,subQ5,subQ6]),TDD([makeQuery(id+"F5.boolean.opBoolean","INTERSECT",VERTEX,{"disambiguationData":[OD(0.0)],"derivedFrom":[makeQuery(id+"F1.opExtrude","CAP_FACE",FACE,{"disambiguationData":[OSD([subQ0,subQ1,subQ2,subQ3])],"isStart":false}),makeQuery(id+"F5.opRevolve","SWEPT_FACE",FACE,{"disambiguationData":[OSD([subQ4,subQ5])]}),makeQuery(id+"F5.opRevolve","SWEPT_FACE",FACE,{"disambiguationData":[OSD([subQ6])]})]})])]});}
            var Q58;
            {var subQ0=sQuery(id+"F0.wireOp",EDGE,"E0.bottom");var subQ1=sQuery(id+"F0.wireOp",EDGE,"E0.top");var subQ2=sQuery(id+"F0.wireOp",EDGE,"E0.left");var subQ3=sQuery(id+"F0.wireOp",EDGE,"E0.right");var subQ4=sQuery(id+"F4.wireOp",EDGE,"E15.MirrorCS");var subQ5=sQuery(id+"F4.wireOp",EDGE,"E17.MirrorCS");Q58=makeQuery(id+"F14.opExtrude","SWEPT_EDGE",EDGE,{"disambiguationData":[OSD([subQ0,subQ1,subQ2,subQ3,subQ4,subQ5]),TDD([makeQuery(id+"F5.boolean.opBoolean","INTERSECT",VERTEX,{"disambiguationData":[OD(0.0)],"derivedFrom":[makeQuery(id+"F1.opExtrude","CAP_FACE",FACE,{"disambiguationData":[OSD([subQ0,subQ1,subQ2,subQ3])],"isStart":false}),makeQuery(id+"F5.opRevolve","SWEPT_FACE",FACE,{"disambiguationData":[OSD([subQ4])]}),makeQuery(id+"F5.opRevolve","SWEPT_FACE",FACE,{"disambiguationData":[OSD([subQ5])]})]})])]});}
            var Q59;
            {var subQ0=sQuery(id+"F0.wireOp",EDGE,"E0.bottom");var subQ1=sQuery(id+"F0.wireOp",EDGE,"E0.top");var subQ2=sQuery(id+"F0.wireOp",EDGE,"E0.left");var subQ3=sQuery(id+"F0.wireOp",EDGE,"E0.right");var subQ4=sQuery(id+"F4.wireOp",EDGE,"E16.MirrorCS");var subQ5=sQuery(id+"F4.wireOp",EDGE,"E17.MirrorCS");Q59=makeQuery(id+"F14.opExtrude","SWEPT_EDGE",EDGE,{"disambiguationData":[OSD([subQ0,subQ1,subQ2,subQ3,subQ4,subQ5]),TDD([makeQuery(id+"F5.boolean.opBoolean","INTERSECT",VERTEX,{"disambiguationData":[OD(0.0)],"derivedFrom":[makeQuery(id+"F1.opExtrude","CAP_FACE",FACE,{"disambiguationData":[OSD([subQ0,subQ1,subQ2,subQ3])],"isStart":false}),makeQuery(id+"F5.opRevolve","SWEPT_FACE",FACE,{"disambiguationData":[OSD([subQ4])]}),makeQuery(id+"F5.opRevolve","SWEPT_FACE",FACE,{"disambiguationData":[OSD([subQ5])]})]})])]});}
            var Q60;
            {var subQ0=sQuery(id+"F0.wireOp",EDGE,"E0.bottom");var subQ1=sQuery(id+"F0.wireOp",EDGE,"E0.top");var subQ2=sQuery(id+"F0.wireOp",EDGE,"E0.left");var subQ3=sQuery(id+"F0.wireOp",EDGE,"E0.right");var subQ4=sQuery(id+"F8.wireOp",EDGE,"E31");var subQ5=sQuery(id+"F8.wireOp",EDGE,"E32.MirrorCS");var subQ6=sQuery(id+"F8.wireOp",EDGE,"E33.MirrorCS");Q60=makeQuery(id+"F14.opExtrude","SWEPT_EDGE",EDGE,{"disambiguationData":[OSD([subQ0,subQ1,subQ2,subQ3,subQ4,subQ5,subQ6]),TDD([makeQuery(id+"F9.boolean.opBoolean","INTERSECT",VERTEX,{"disambiguationData":[OD(0.0)],"derivedFrom":[makeQuery(id+"F1.opExtrude","CAP_FACE",FACE,{"disambiguationData":[OSD([subQ0,subQ1,subQ2,subQ3])],"isStart":false}),makeQuery(id+"F9.opRevolve","SWEPT_FACE",FACE,{"disambiguationData":[OSD([subQ4,subQ5])]}),makeQuery(id+"F9.opRevolve","SWEPT_FACE",FACE,{"disambiguationData":[OSD([subQ6])]})]})])]});}
            var Q61;
            {var subQ0=sQuery(id+"F0.wireOp",EDGE,"E0.bottom");var subQ1=sQuery(id+"F0.wireOp",EDGE,"E0.top");var subQ2=sQuery(id+"F0.wireOp",EDGE,"E0.left");var subQ3=sQuery(id+"F0.wireOp",EDGE,"E0.right");var subQ4=sQuery(id+"F8.wireOp",EDGE,"E33.MirrorCS");var subQ5=sQuery(id+"F8.wireOp",EDGE,"E35.MirrorCS");Q61=makeQuery(id+"F14.opExtrude","SWEPT_EDGE",EDGE,{"disambiguationData":[OSD([subQ0,subQ1,subQ2,subQ3,subQ4,subQ5]),TDD([makeQuery(id+"F9.boolean.opBoolean","INTERSECT",VERTEX,{"disambiguationData":[OD(0.0)],"derivedFrom":[makeQuery(id+"F1.opExtrude","CAP_FACE",FACE,{"disambiguationData":[OSD([subQ0,subQ1,subQ2,subQ3])],"isStart":false}),makeQuery(id+"F9.opRevolve","SWEPT_FACE",FACE,{"disambiguationData":[OSD([subQ4])]}),makeQuery(id+"F9.opRevolve","SWEPT_FACE",FACE,{"disambiguationData":[OSD([subQ5])]})]})])]});}
            var Q62;
            {var subQ0=sQuery(id+"F0.wireOp",EDGE,"E0.bottom");var subQ1=sQuery(id+"F0.wireOp",EDGE,"E0.top");var subQ2=sQuery(id+"F0.wireOp",EDGE,"E0.left");var subQ3=sQuery(id+"F0.wireOp",EDGE,"E0.right");var subQ4=sQuery(id+"F8.wireOp",EDGE,"E34.MirrorCS");var subQ5=sQuery(id+"F8.wireOp",EDGE,"E35.MirrorCS");Q62=makeQuery(id+"F14.opExtrude","SWEPT_EDGE",EDGE,{"disambiguationData":[OSD([subQ0,subQ1,subQ2,subQ3,subQ4,subQ5]),TDD([makeQuery(id+"F9.boolean.opBoolean","INTERSECT",VERTEX,{"disambiguationData":[OD(0.0)],"derivedFrom":[makeQuery(id+"F1.opExtrude","CAP_FACE",FACE,{"disambiguationData":[OSD([subQ0,subQ1,subQ2,subQ3])],"isStart":false}),makeQuery(id+"F9.opRevolve","SWEPT_FACE",FACE,{"disambiguationData":[OSD([subQ4])]}),makeQuery(id+"F9.opRevolve","SWEPT_FACE",FACE,{"disambiguationData":[OSD([subQ5])]})]})])]});}
            var Q63;
            {var subQ0=sQuery(id+"F0.wireOp",EDGE,"E0.bottom");var subQ1=sQuery(id+"F0.wireOp",EDGE,"E0.top");var subQ2=sQuery(id+"F0.wireOp",EDGE,"E0.left");var subQ3=sQuery(id+"F0.wireOp",EDGE,"E0.right");var subQ4=sQuery(id+"F8.wireOp",EDGE,"E34.MirrorCS");var subQ5=sQuery(id+"F8.wireOp",EDGE,"E35.MirrorCS");Q63=makeQuery(id+"F14.opExtrude","SWEPT_EDGE",EDGE,{"disambiguationData":[OSD([subQ0,subQ1,subQ2,subQ3,subQ4,subQ5]),TDD([makeQuery(id+"F9.boolean.opBoolean","INTERSECT",VERTEX,{"disambiguationData":[OD(1.0)],"derivedFrom":[makeQuery(id+"F1.opExtrude","CAP_FACE",FACE,{"disambiguationData":[OSD([subQ0,subQ1,subQ2,subQ3])],"isStart":false}),makeQuery(id+"F9.opRevolve","SWEPT_FACE",FACE,{"disambiguationData":[OSD([subQ4])]}),makeQuery(id+"F9.opRevolve","SWEPT_FACE",FACE,{"disambiguationData":[OSD([subQ5])]})]})])]});}
            var Q64;
            {var subQ0=sQuery(id+"F0.wireOp",EDGE,"E0.bottom");var subQ1=sQuery(id+"F0.wireOp",EDGE,"E0.top");var subQ2=sQuery(id+"F0.wireOp",EDGE,"E0.left");var subQ3=sQuery(id+"F0.wireOp",EDGE,"E0.right");var subQ4=sQuery(id+"F8.wireOp",EDGE,"E33.MirrorCS");var subQ5=sQuery(id+"F8.wireOp",EDGE,"E35.MirrorCS");Q64=makeQuery(id+"F14.opExtrude","SWEPT_EDGE",EDGE,{"disambiguationData":[OSD([subQ0,subQ1,subQ2,subQ3,subQ4,subQ5]),TDD([makeQuery(id+"F9.boolean.opBoolean","INTERSECT",VERTEX,{"disambiguationData":[OD(1.0)],"derivedFrom":[makeQuery(id+"F1.opExtrude","CAP_FACE",FACE,{"disambiguationData":[OSD([subQ0,subQ1,subQ2,subQ3])],"isStart":false}),makeQuery(id+"F9.opRevolve","SWEPT_FACE",FACE,{"disambiguationData":[OSD([subQ4])]}),makeQuery(id+"F9.opRevolve","SWEPT_FACE",FACE,{"disambiguationData":[OSD([subQ5])]})]})])]});}
            var Q65;
            {var subQ0=sQuery(id+"F0.wireOp",EDGE,"E0.bottom");var subQ1=sQuery(id+"F0.wireOp",EDGE,"E0.top");var subQ2=sQuery(id+"F0.wireOp",EDGE,"E0.left");var subQ3=sQuery(id+"F0.wireOp",EDGE,"E0.right");var subQ4=sQuery(id+"F8.wireOp",EDGE,"E31");var subQ5=sQuery(id+"F8.wireOp",EDGE,"E32.MirrorCS");var subQ6=sQuery(id+"F8.wireOp",EDGE,"E33.MirrorCS");Q65=makeQuery(id+"F14.opExtrude","SWEPT_EDGE",EDGE,{"disambiguationData":[OSD([subQ0,subQ1,subQ2,subQ3,subQ4,subQ5,subQ6]),TDD([makeQuery(id+"F9.boolean.opBoolean","INTERSECT",VERTEX,{"disambiguationData":[OD(1.0)],"derivedFrom":[makeQuery(id+"F1.opExtrude","CAP_FACE",FACE,{"disambiguationData":[OSD([subQ0,subQ1,subQ2,subQ3])],"isStart":false}),makeQuery(id+"F9.opRevolve","SWEPT_FACE",FACE,{"disambiguationData":[OSD([subQ4,subQ5])]}),makeQuery(id+"F9.opRevolve","SWEPT_FACE",FACE,{"disambiguationData":[OSD([subQ6])]})]})])]});}
            var Q66;
            {var subQ0=sQuery(id+"F0.wireOp",EDGE,"E0.bottom");var subQ1=sQuery(id+"F0.wireOp",EDGE,"E0.top");var subQ2=sQuery(id+"F0.wireOp",EDGE,"E0.left");var subQ3=sQuery(id+"F0.wireOp",EDGE,"E0.right");var subQ4=sQuery(id+"F10.wireOp",EDGE,"E43.MirrorCS");var subQ5=sQuery(id+"F10.wireOp",EDGE,"E44.MirrorCS");Q66=makeQuery(id+"F14.opExtrude","SWEPT_EDGE",EDGE,{"disambiguationData":[OSD([subQ0,subQ1,subQ2,subQ3,subQ4,subQ5]),TDD([makeQuery(id+"F11.boolean.opBoolean","INTERSECT",VERTEX,{"disambiguationData":[OD(1.0)],"derivedFrom":[makeQuery(id+"F1.opExtrude","CAP_FACE",FACE,{"disambiguationData":[OSD([subQ0,subQ1,subQ2,subQ3])],"isStart":false}),makeQuery(id+"F11.opRevolve","SWEPT_FACE",FACE,{"disambiguationData":[OSD([subQ4])]}),makeQuery(id+"F11.opRevolve","SWEPT_FACE",FACE,{"disambiguationData":[OSD([subQ5])]})]})])]});}
            var Q67;
            {var subQ0=sQuery(id+"F0.wireOp",EDGE,"E0.bottom");var subQ1=sQuery(id+"F0.wireOp",EDGE,"E0.top");var subQ2=sQuery(id+"F0.wireOp",EDGE,"E0.left");var subQ3=sQuery(id+"F0.wireOp",EDGE,"E0.right");var subQ4=sQuery(id+"F10.wireOp",EDGE,"E42.MirrorCS");var subQ5=sQuery(id+"F10.wireOp",EDGE,"E44.MirrorCS");Q67=makeQuery(id+"F14.opExtrude","SWEPT_EDGE",EDGE,{"disambiguationData":[OSD([subQ0,subQ1,subQ2,subQ3,subQ4,subQ5]),TDD([makeQuery(id+"F11.boolean.opBoolean","INTERSECT",VERTEX,{"disambiguationData":[OD(1.0)],"derivedFrom":[makeQuery(id+"F1.opExtrude","CAP_FACE",FACE,{"disambiguationData":[OSD([subQ0,subQ1,subQ2,subQ3])],"isStart":false}),makeQuery(id+"F11.opRevolve","SWEPT_FACE",FACE,{"disambiguationData":[OSD([subQ4])]}),makeQuery(id+"F11.opRevolve","SWEPT_FACE",FACE,{"disambiguationData":[OSD([subQ5])]})]})])]});}
            var Q68;
            {var subQ0=sQuery(id+"F0.wireOp",EDGE,"E0.bottom");var subQ1=sQuery(id+"F0.wireOp",EDGE,"E0.top");var subQ2=sQuery(id+"F0.wireOp",EDGE,"E0.left");var subQ3=sQuery(id+"F0.wireOp",EDGE,"E0.right");var subQ4=sQuery(id+"F10.wireOp",EDGE,"E40");var subQ5=sQuery(id+"F10.wireOp",EDGE,"E41.MirrorCS");var subQ6=sQuery(id+"F10.wireOp",EDGE,"E42.MirrorCS");Q68=makeQuery(id+"F14.opExtrude","SWEPT_EDGE",EDGE,{"disambiguationData":[OSD([subQ0,subQ1,subQ2,subQ3,subQ4,subQ5,subQ6]),TDD([makeQuery(id+"F11.boolean.opBoolean","INTERSECT",VERTEX,{"disambiguationData":[OD(1.0)],"derivedFrom":[makeQuery(id+"F1.opExtrude","CAP_FACE",FACE,{"disambiguationData":[OSD([subQ0,subQ1,subQ2,subQ3])],"isStart":false}),makeQuery(id+"F11.opRevolve","SWEPT_FACE",FACE,{"disambiguationData":[OSD([subQ4,subQ5])]}),makeQuery(id+"F11.opRevolve","SWEPT_FACE",FACE,{"disambiguationData":[OSD([subQ6])]})]})])]});}
            var Q69;
            {var subQ0=sQuery(id+"F0.wireOp",EDGE,"E0.bottom");var subQ1=sQuery(id+"F0.wireOp",EDGE,"E0.top");var subQ2=sQuery(id+"F0.wireOp",EDGE,"E0.left");var subQ3=sQuery(id+"F0.wireOp",EDGE,"E0.right");var subQ4=sQuery(id+"F10.wireOp",EDGE,"E43.MirrorCS");var subQ5=sQuery(id+"F10.wireOp",EDGE,"E44.MirrorCS");Q69=makeQuery(id+"F14.opExtrude","SWEPT_EDGE",EDGE,{"disambiguationData":[OSD([subQ0,subQ1,subQ2,subQ3,subQ4,subQ5]),TDD([makeQuery(id+"F11.boolean.opBoolean","INTERSECT",VERTEX,{"disambiguationData":[OD(0.0)],"derivedFrom":[makeQuery(id+"F1.opExtrude","CAP_FACE",FACE,{"disambiguationData":[OSD([subQ0,subQ1,subQ2,subQ3])],"isStart":false}),makeQuery(id+"F11.opRevolve","SWEPT_FACE",FACE,{"disambiguationData":[OSD([subQ4])]}),makeQuery(id+"F11.opRevolve","SWEPT_FACE",FACE,{"disambiguationData":[OSD([subQ5])]})]})])]});}
            var Q70;
            {var subQ0=sQuery(id+"F0.wireOp",EDGE,"E0.bottom");var subQ1=sQuery(id+"F0.wireOp",EDGE,"E0.top");var subQ2=sQuery(id+"F0.wireOp",EDGE,"E0.left");var subQ3=sQuery(id+"F0.wireOp",EDGE,"E0.right");var subQ4=sQuery(id+"F10.wireOp",EDGE,"E42.MirrorCS");var subQ5=sQuery(id+"F10.wireOp",EDGE,"E44.MirrorCS");Q70=makeQuery(id+"F14.opExtrude","SWEPT_EDGE",EDGE,{"disambiguationData":[OSD([subQ0,subQ1,subQ2,subQ3,subQ4,subQ5]),TDD([makeQuery(id+"F11.boolean.opBoolean","INTERSECT",VERTEX,{"disambiguationData":[OD(0.0)],"derivedFrom":[makeQuery(id+"F1.opExtrude","CAP_FACE",FACE,{"disambiguationData":[OSD([subQ0,subQ1,subQ2,subQ3])],"isStart":false}),makeQuery(id+"F11.opRevolve","SWEPT_FACE",FACE,{"disambiguationData":[OSD([subQ4])]}),makeQuery(id+"F11.opRevolve","SWEPT_FACE",FACE,{"disambiguationData":[OSD([subQ5])]})]})])]});}
            var Q71;
            {var subQ0=sQuery(id+"F0.wireOp",EDGE,"E0.bottom");var subQ1=sQuery(id+"F0.wireOp",EDGE,"E0.top");var subQ2=sQuery(id+"F0.wireOp",EDGE,"E0.left");var subQ3=sQuery(id+"F0.wireOp",EDGE,"E0.right");var subQ4=sQuery(id+"F10.wireOp",EDGE,"E40");var subQ5=sQuery(id+"F10.wireOp",EDGE,"E41.MirrorCS");var subQ6=sQuery(id+"F10.wireOp",EDGE,"E42.MirrorCS");Q71=makeQuery(id+"F14.opExtrude","SWEPT_EDGE",EDGE,{"disambiguationData":[OSD([subQ0,subQ1,subQ2,subQ3,subQ4,subQ5,subQ6]),TDD([makeQuery(id+"F11.boolean.opBoolean","INTERSECT",VERTEX,{"disambiguationData":[OD(0.0)],"derivedFrom":[makeQuery(id+"F1.opExtrude","CAP_FACE",FACE,{"disambiguationData":[OSD([subQ0,subQ1,subQ2,subQ3])],"isStart":false}),makeQuery(id+"F11.opRevolve","SWEPT_FACE",FACE,{"disambiguationData":[OSD([subQ4,subQ5])]}),makeQuery(id+"F11.opRevolve","SWEPT_FACE",FACE,{"disambiguationData":[OSD([subQ6])]})]})])]});}
            var Q72;
            {var subQ0=sQuery(id+"F0.wireOp",EDGE,"E0.bottom");var subQ1=sQuery(id+"F0.wireOp",EDGE,"E0.top");var subQ2=sQuery(id+"F0.wireOp",EDGE,"E0.left");var subQ3=sQuery(id+"F0.wireOp",EDGE,"E0.right");var subQ4=sQuery(id+"F10.wireOp",EDGE,"E39");var subQ5=sQuery(id+"F10.wireOp",EDGE,"E40");var subQ6=sQuery(id+"F10.wireOp",EDGE,"E41.MirrorCS");Q72=makeQuery(id+"F14.opExtrude","SWEPT_EDGE",EDGE,{"disambiguationData":[OSD([subQ0,subQ1,subQ2,subQ3,subQ4,subQ5,subQ6]),TDD([makeQuery(id+"F11.boolean.opBoolean","INTERSECT",VERTEX,{"disambiguationData":[OD(1.0)],"derivedFrom":[makeQuery(id+"F1.opExtrude","CAP_FACE",FACE,{"disambiguationData":[OSD([subQ0,subQ1,subQ2,subQ3])],"isStart":false}),makeQuery(id+"F11.opRevolve","SWEPT_FACE",FACE,{"disambiguationData":[OSD([subQ4])]}),makeQuery(id+"F11.opRevolve","SWEPT_FACE",FACE,{"disambiguationData":[OSD([subQ5,subQ6])]})]})])]});}
            var Q73;
            {var subQ0=sQuery(id+"F0.wireOp",EDGE,"E0.bottom");var subQ1=sQuery(id+"F0.wireOp",EDGE,"E0.top");var subQ2=sQuery(id+"F0.wireOp",EDGE,"E0.left");var subQ3=sQuery(id+"F0.wireOp",EDGE,"E0.right");var subQ4=sQuery(id+"F10.wireOp",EDGE,"E38");var subQ5=sQuery(id+"F10.wireOp",EDGE,"E39");Q73=makeQuery(id+"F14.opExtrude","SWEPT_EDGE",EDGE,{"disambiguationData":[OSD([subQ0,subQ1,subQ2,subQ3,subQ4,subQ5]),TDD([makeQuery(id+"F11.boolean.opBoolean","INTERSECT",VERTEX,{"disambiguationData":[OD(1.0)],"derivedFrom":[makeQuery(id+"F1.opExtrude","CAP_FACE",FACE,{"disambiguationData":[OSD([subQ0,subQ1,subQ2,subQ3])],"isStart":false}),makeQuery(id+"F11.opRevolve","SWEPT_FACE",FACE,{"disambiguationData":[OSD([subQ4])]}),makeQuery(id+"F11.opRevolve","SWEPT_FACE",FACE,{"disambiguationData":[OSD([subQ5])]})]})])]});}
            var Q74;
            {var subQ0=sQuery(id+"F0.wireOp",EDGE,"E0.bottom");var subQ1=sQuery(id+"F0.wireOp",EDGE,"E0.top");var subQ2=sQuery(id+"F0.wireOp",EDGE,"E0.left");var subQ3=sQuery(id+"F0.wireOp",EDGE,"E0.right");var subQ4=sQuery(id+"F10.wireOp",EDGE,"E37");var subQ5=sQuery(id+"F10.wireOp",EDGE,"E38");Q74=makeQuery(id+"F14.opExtrude","SWEPT_EDGE",EDGE,{"disambiguationData":[OSD([subQ0,subQ1,subQ2,subQ3,subQ4,subQ5]),TDD([makeQuery(id+"F11.boolean.opBoolean","INTERSECT",VERTEX,{"disambiguationData":[OD(1.0)],"derivedFrom":[makeQuery(id+"F1.opExtrude","CAP_FACE",FACE,{"disambiguationData":[OSD([subQ0,subQ1,subQ2,subQ3])],"isStart":false}),makeQuery(id+"F11.opRevolve","SWEPT_FACE",FACE,{"disambiguationData":[OSD([subQ4])]}),makeQuery(id+"F11.opRevolve","SWEPT_FACE",FACE,{"disambiguationData":[OSD([subQ5])]})]})])]});}
            var Q75;
            {var subQ0=sQuery(id+"F0.wireOp",EDGE,"E0.bottom");var subQ1=sQuery(id+"F0.wireOp",EDGE,"E0.top");var subQ2=sQuery(id+"F0.wireOp",EDGE,"E0.left");var subQ3=sQuery(id+"F0.wireOp",EDGE,"E0.right");var subQ4=sQuery(id+"F8.wireOp",EDGE,"E30");var subQ5=sQuery(id+"F8.wireOp",EDGE,"E31");var subQ6=sQuery(id+"F8.wireOp",EDGE,"E32.MirrorCS");Q75=makeQuery(id+"F14.opExtrude","SWEPT_EDGE",EDGE,{"disambiguationData":[OSD([subQ0,subQ1,subQ2,subQ3,subQ4,subQ5,subQ6]),TDD([makeQuery(id+"F9.boolean.opBoolean","INTERSECT",VERTEX,{"disambiguationData":[OD(1.0)],"derivedFrom":[makeQuery(id+"F1.opExtrude","CAP_FACE",FACE,{"disambiguationData":[OSD([subQ0,subQ1,subQ2,subQ3])],"isStart":false}),makeQuery(id+"F9.opRevolve","SWEPT_FACE",FACE,{"disambiguationData":[OSD([subQ4])]}),makeQuery(id+"F9.opRevolve","SWEPT_FACE",FACE,{"disambiguationData":[OSD([subQ5,subQ6])]})]})])]});}
            var Q76;
            {var subQ0=sQuery(id+"F0.wireOp",EDGE,"E0.bottom");var subQ1=sQuery(id+"F0.wireOp",EDGE,"E0.top");var subQ2=sQuery(id+"F0.wireOp",EDGE,"E0.left");var subQ3=sQuery(id+"F0.wireOp",EDGE,"E0.right");var subQ4=sQuery(id+"F8.wireOp",EDGE,"E29");var subQ5=sQuery(id+"F8.wireOp",EDGE,"E30");Q76=makeQuery(id+"F14.opExtrude","SWEPT_EDGE",EDGE,{"disambiguationData":[OSD([subQ0,subQ1,subQ2,subQ3,subQ4,subQ5]),TDD([makeQuery(id+"F9.boolean.opBoolean","INTERSECT",VERTEX,{"disambiguationData":[OD(1.0)],"derivedFrom":[makeQuery(id+"F1.opExtrude","CAP_FACE",FACE,{"disambiguationData":[OSD([subQ0,subQ1,subQ2,subQ3])],"isStart":false}),makeQuery(id+"F9.opRevolve","SWEPT_FACE",FACE,{"disambiguationData":[OSD([subQ4])]}),makeQuery(id+"F9.opRevolve","SWEPT_FACE",FACE,{"disambiguationData":[OSD([subQ5])]})]})])]});}
            var Q77;
            {var subQ0=sQuery(id+"F0.wireOp",EDGE,"E0.bottom");var subQ1=sQuery(id+"F0.wireOp",EDGE,"E0.top");var subQ2=sQuery(id+"F0.wireOp",EDGE,"E0.left");var subQ3=sQuery(id+"F0.wireOp",EDGE,"E0.right");var subQ4=sQuery(id+"F8.wireOp",EDGE,"E28");var subQ5=sQuery(id+"F8.wireOp",EDGE,"E29");Q77=makeQuery(id+"F14.opExtrude","SWEPT_EDGE",EDGE,{"disambiguationData":[OSD([subQ0,subQ1,subQ2,subQ3,subQ4,subQ5]),TDD([makeQuery(id+"F9.boolean.opBoolean","INTERSECT",VERTEX,{"disambiguationData":[OD(1.0)],"derivedFrom":[makeQuery(id+"F1.opExtrude","CAP_FACE",FACE,{"disambiguationData":[OSD([subQ0,subQ1,subQ2,subQ3])],"isStart":false}),makeQuery(id+"F9.opRevolve","SWEPT_FACE",FACE,{"disambiguationData":[OSD([subQ4])]}),makeQuery(id+"F9.opRevolve","SWEPT_FACE",FACE,{"disambiguationData":[OSD([subQ5])]})]})])]});}
            var Q78;
            {var subQ0=sQuery(id+"F0.wireOp",EDGE,"E0.bottom");var subQ1=sQuery(id+"F0.wireOp",EDGE,"E0.top");var subQ2=sQuery(id+"F0.wireOp",EDGE,"E0.left");var subQ3=sQuery(id+"F0.wireOp",EDGE,"E0.right");var subQ4=sQuery(id+"F8.wireOp",EDGE,"E30");var subQ5=sQuery(id+"F8.wireOp",EDGE,"E31");var subQ6=sQuery(id+"F8.wireOp",EDGE,"E32.MirrorCS");Q78=makeQuery(id+"F14.opExtrude","SWEPT_EDGE",EDGE,{"disambiguationData":[OSD([subQ0,subQ1,subQ2,subQ3,subQ4,subQ5,subQ6]),TDD([makeQuery(id+"F9.boolean.opBoolean","INTERSECT",VERTEX,{"disambiguationData":[OD(0.0)],"derivedFrom":[makeQuery(id+"F1.opExtrude","CAP_FACE",FACE,{"disambiguationData":[OSD([subQ0,subQ1,subQ2,subQ3])],"isStart":false}),makeQuery(id+"F9.opRevolve","SWEPT_FACE",FACE,{"disambiguationData":[OSD([subQ4])]}),makeQuery(id+"F9.opRevolve","SWEPT_FACE",FACE,{"disambiguationData":[OSD([subQ5,subQ6])]})]})])]});}
            var Q79;
            {var subQ0=sQuery(id+"F0.wireOp",EDGE,"E0.bottom");var subQ1=sQuery(id+"F0.wireOp",EDGE,"E0.top");var subQ2=sQuery(id+"F0.wireOp",EDGE,"E0.left");var subQ3=sQuery(id+"F0.wireOp",EDGE,"E0.right");var subQ4=sQuery(id+"F8.wireOp",EDGE,"E29");var subQ5=sQuery(id+"F8.wireOp",EDGE,"E30");Q79=makeQuery(id+"F14.opExtrude","SWEPT_EDGE",EDGE,{"disambiguationData":[OSD([subQ0,subQ1,subQ2,subQ3,subQ4,subQ5]),TDD([makeQuery(id+"F9.boolean.opBoolean","INTERSECT",VERTEX,{"disambiguationData":[OD(0.0)],"derivedFrom":[makeQuery(id+"F1.opExtrude","CAP_FACE",FACE,{"disambiguationData":[OSD([subQ0,subQ1,subQ2,subQ3])],"isStart":false}),makeQuery(id+"F9.opRevolve","SWEPT_FACE",FACE,{"disambiguationData":[OSD([subQ4])]}),makeQuery(id+"F9.opRevolve","SWEPT_FACE",FACE,{"disambiguationData":[OSD([subQ5])]})]})])]});}
            var Q80;
            {var subQ0=sQuery(id+"F0.wireOp",EDGE,"E0.bottom");var subQ1=sQuery(id+"F0.wireOp",EDGE,"E0.top");var subQ2=sQuery(id+"F0.wireOp",EDGE,"E0.left");var subQ3=sQuery(id+"F0.wireOp",EDGE,"E0.right");var subQ4=sQuery(id+"F8.wireOp",EDGE,"E28");var subQ5=sQuery(id+"F8.wireOp",EDGE,"E29");Q80=makeQuery(id+"F14.opExtrude","SWEPT_EDGE",EDGE,{"disambiguationData":[OSD([subQ0,subQ1,subQ2,subQ3,subQ4,subQ5]),TDD([makeQuery(id+"F9.boolean.opBoolean","INTERSECT",VERTEX,{"disambiguationData":[OD(0.0)],"derivedFrom":[makeQuery(id+"F1.opExtrude","CAP_FACE",FACE,{"disambiguationData":[OSD([subQ0,subQ1,subQ2,subQ3])],"isStart":false}),makeQuery(id+"F9.opRevolve","SWEPT_FACE",FACE,{"disambiguationData":[OSD([subQ4])]}),makeQuery(id+"F9.opRevolve","SWEPT_FACE",FACE,{"disambiguationData":[OSD([subQ5])]})]})])]});}
            var Q81;
            {var subQ0=sQuery(id+"F0.wireOp",EDGE,"E0.bottom");var subQ1=sQuery(id+"F0.wireOp",EDGE,"E0.top");var subQ2=sQuery(id+"F0.wireOp",EDGE,"E0.left");var subQ3=sQuery(id+"F0.wireOp",EDGE,"E0.right");var subQ4=sQuery(id+"F10.wireOp",EDGE,"E37");var subQ5=sQuery(id+"F10.wireOp",EDGE,"E38");Q81=makeQuery(id+"F14.opExtrude","SWEPT_EDGE",EDGE,{"disambiguationData":[OSD([subQ0,subQ1,subQ2,subQ3,subQ4,subQ5]),TDD([makeQuery(id+"F11.boolean.opBoolean","INTERSECT",VERTEX,{"disambiguationData":[OD(0.0)],"derivedFrom":[makeQuery(id+"F1.opExtrude","CAP_FACE",FACE,{"disambiguationData":[OSD([subQ0,subQ1,subQ2,subQ3])],"isStart":false}),makeQuery(id+"F11.opRevolve","SWEPT_FACE",FACE,{"disambiguationData":[OSD([subQ4])]}),makeQuery(id+"F11.opRevolve","SWEPT_FACE",FACE,{"disambiguationData":[OSD([subQ5])]})]})])]});}
            var Q82;
            {var subQ0=sQuery(id+"F0.wireOp",EDGE,"E0.bottom");var subQ1=sQuery(id+"F0.wireOp",EDGE,"E0.top");var subQ2=sQuery(id+"F0.wireOp",EDGE,"E0.left");var subQ3=sQuery(id+"F0.wireOp",EDGE,"E0.right");var subQ4=sQuery(id+"F10.wireOp",EDGE,"E38");var subQ5=sQuery(id+"F10.wireOp",EDGE,"E39");Q82=makeQuery(id+"F14.opExtrude","SWEPT_EDGE",EDGE,{"disambiguationData":[OSD([subQ0,subQ1,subQ2,subQ3,subQ4,subQ5]),TDD([makeQuery(id+"F11.boolean.opBoolean","INTERSECT",VERTEX,{"disambiguationData":[OD(0.0)],"derivedFrom":[makeQuery(id+"F1.opExtrude","CAP_FACE",FACE,{"disambiguationData":[OSD([subQ0,subQ1,subQ2,subQ3])],"isStart":false}),makeQuery(id+"F11.opRevolve","SWEPT_FACE",FACE,{"disambiguationData":[OSD([subQ4])]}),makeQuery(id+"F11.opRevolve","SWEPT_FACE",FACE,{"disambiguationData":[OSD([subQ5])]})]})])]});}
            var Q83;
            {var subQ0=sQuery(id+"F0.wireOp",EDGE,"E0.bottom");var subQ1=sQuery(id+"F0.wireOp",EDGE,"E0.top");var subQ2=sQuery(id+"F0.wireOp",EDGE,"E0.left");var subQ3=sQuery(id+"F0.wireOp",EDGE,"E0.right");var subQ4=sQuery(id+"F10.wireOp",EDGE,"E39");var subQ5=sQuery(id+"F10.wireOp",EDGE,"E40");var subQ6=sQuery(id+"F10.wireOp",EDGE,"E41.MirrorCS");Q83=makeQuery(id+"F14.opExtrude","SWEPT_EDGE",EDGE,{"disambiguationData":[OSD([subQ0,subQ1,subQ2,subQ3,subQ4,subQ5,subQ6]),TDD([makeQuery(id+"F11.boolean.opBoolean","INTERSECT",VERTEX,{"disambiguationData":[OD(0.0)],"derivedFrom":[makeQuery(id+"F1.opExtrude","CAP_FACE",FACE,{"disambiguationData":[OSD([subQ0,subQ1,subQ2,subQ3])],"isStart":false}),makeQuery(id+"F11.opRevolve","SWEPT_FACE",FACE,{"disambiguationData":[OSD([subQ4])]}),makeQuery(id+"F11.opRevolve","SWEPT_FACE",FACE,{"disambiguationData":[OSD([subQ5,subQ6])]})]})])]});}
            var Q84;
            Q84=makeQuery(id+"F11.boolean.opBoolean","COPY",EDGE,{"derivedFrom":makeQuery(id+"F11.opRevolve","SWEPT_EDGE",EDGE,{"disambiguationData":[OSD([sQuery(id+"F10.wireOp",EDGE,"E37"),sQuery(id+"F10.wireOp",EDGE,"E38")])]})});
            var Q85;
            Q85=makeQuery(id+"F9.boolean.opBoolean","COPY",EDGE,{"derivedFrom":makeQuery(id+"F9.opRevolve","SWEPT_EDGE",EDGE,{"disambiguationData":[OSD([sQuery(id+"F8.wireOp",EDGE,"E28"),sQuery(id+"F8.wireOp",EDGE,"E29")])]})});
            var Q86;
            Q86=makeQuery(id+"F7.boolean.opBoolean","COPY",EDGE,{"derivedFrom":makeQuery(id+"F7.opRevolve","SWEPT_EDGE",EDGE,{"disambiguationData":[OSD([sQuery(id+"F6.wireOp",EDGE,"E19"),sQuery(id+"F6.wireOp",EDGE,"E20")])]})});
            var Q87;
            Q87=makeQuery(id+"F5.boolean.opBoolean","COPY",EDGE,{"derivedFrom":makeQuery(id+"F5.opRevolve","SWEPT_EDGE",EDGE,{"disambiguationData":[OSD([sQuery(id+"F4.wireOp",EDGE,"E10"),sQuery(id+"F4.wireOp",EDGE,"E11")])]})});
            var Q88;
            Q88=makeQuery(id+"F3.boolean.opBoolean","COPY",EDGE,{"derivedFrom":makeQuery(id+"F3.opRevolve","SWEPT_EDGE",EDGE,{"disambiguationData":[OSD([sQuery(id+"F2.wireOp",EDGE,"E1"),sQuery(id+"F2.wireOp",EDGE,"E2")])]})});
            var Q89;
            Q89=makeQuery(id+"F3.boolean.opBoolean","COPY",EDGE,{"derivedFrom":makeQuery(id+"F3.opRevolve","SWEPT_EDGE",EDGE,{"disambiguationData":[OSD([sQuery(id+"F2.wireOp",EDGE,"E7.MirrorCS"),sQuery(id+"F2.wireOp",EDGE,"E8.MirrorCS")])]})});
            var Q90;
            Q90=makeQuery(id+"F5.boolean.opBoolean","COPY",EDGE,{"derivedFrom":makeQuery(id+"F5.opRevolve","SWEPT_EDGE",EDGE,{"disambiguationData":[OSD([sQuery(id+"F4.wireOp",EDGE,"E16.MirrorCS"),sQuery(id+"F4.wireOp",EDGE,"E17.MirrorCS")])]})});
            var Q91;
            Q91=makeQuery(id+"F7.boolean.opBoolean","COPY",EDGE,{"derivedFrom":makeQuery(id+"F7.opRevolve","SWEPT_EDGE",EDGE,{"disambiguationData":[OSD([sQuery(id+"F6.wireOp",EDGE,"E25.MirrorCS"),sQuery(id+"F6.wireOp",EDGE,"E26.MirrorCS")])]})});
            var Q92;
            Q92=makeQuery(id+"F9.boolean.opBoolean","COPY",EDGE,{"derivedFrom":makeQuery(id+"F9.opRevolve","SWEPT_EDGE",EDGE,{"disambiguationData":[OSD([sQuery(id+"F8.wireOp",EDGE,"E34.MirrorCS"),sQuery(id+"F8.wireOp",EDGE,"E35.MirrorCS")])]})});
            var Q93;
            Q93=makeQuery(id+"F11.boolean.opBoolean","COPY",EDGE,{"derivedFrom":makeQuery(id+"F11.opRevolve","SWEPT_EDGE",EDGE,{"disambiguationData":[OSD([sQuery(id+"F10.wireOp",EDGE,"E43.MirrorCS"),sQuery(id+"F10.wireOp",EDGE,"E44.MirrorCS")])]})});
            fillet(context, id + "F20", {"entities" : qUnion([Q0, Q1, Q2, Q3, Q4, Q5, Q6, Q7, Q8, Q9, Q10, Q11, Q12, Q13, Q14, Q15, Q16, Q17, Q18, Q19, Q20, Q21, Q22, Q23, Q24, Q25, Q26, Q27, Q28, Q29, Q30, Q31, Q32, Q33, Q34, Q35, Q36, Q37, Q38, Q39, Q40, Q41, Q42, Q43, Q44, Q45, Q46, Q47, Q48, Q49, Q50, Q51, Q52, Q53, Q54, Q55, Q56, Q57, Q58, Q59, Q60, Q61, Q62, Q63, Q64, Q65, Q66, Q67, Q68, Q69, Q70, Q71, Q72, Q73, Q74, Q75, Q76, Q77, Q78, Q79, Q80, Q81, Q82, Q83, Q84, Q85, Q86, Q87, Q88, Q89, Q90, Q91, Q92, Q93]), "radius" : 0.32 * mm, "tangentPropagation" : true, "allowEdgeOverflow" : false});
        }
        {
            var Q0;
            Q0=makeQuery(id+"F17.boolean.opBoolean","INTERSECT",EDGE,{"disambiguationData":[OD(0.0)],"derivedFrom":[makeQuery(id+"F14.opExtrude","CAP_FACE",FACE,{"disambiguationData":[OSD([sQuery(id+"F0.wireOp",EDGE,"E0.bottom"),sQuery(id+"F0.wireOp",EDGE,"E0.top"),sQuery(id+"F0.wireOp",EDGE,"E0.left"),sQuery(id+"F0.wireOp",EDGE,"E0.right")])],"isStart":false}),makeQuery(id+"F17.opLoft","SWEPT_FACE",FACE,{"disambiguationData":[OSD([sQuery(id+"F15.wireOp",EDGE,"E46"),sQuery(id+"F16.wireOp",EDGE,"E47")])]})]});
            chamfer(context, id + "F21", {"entities" : qUnion([Q0]), "width" : 0.32 * mm, "tangentPropagation" : true});
        }
    });
